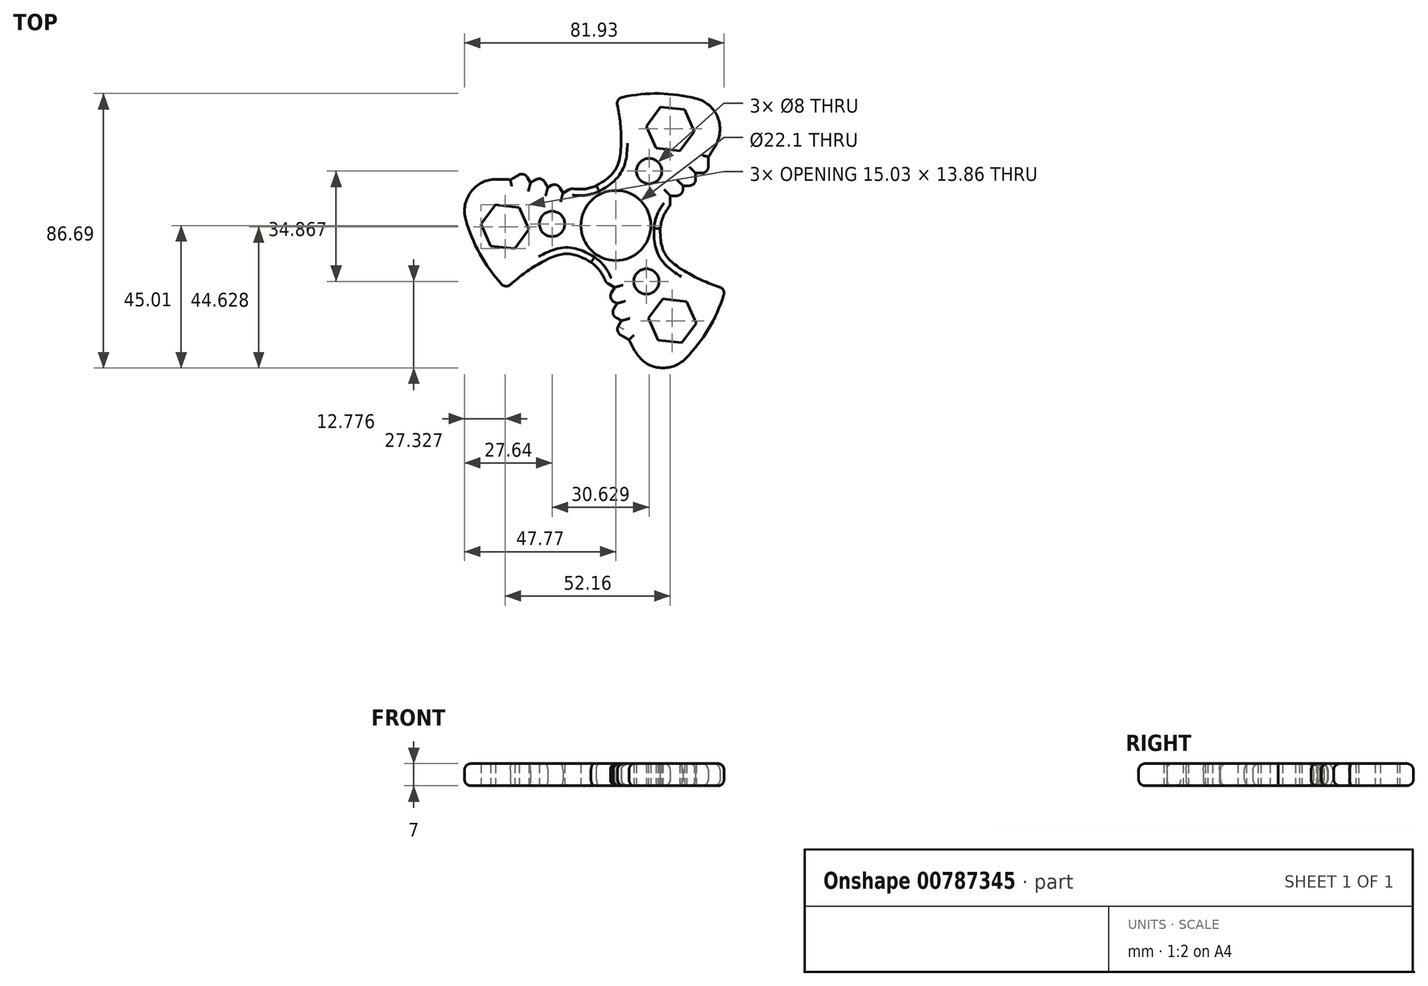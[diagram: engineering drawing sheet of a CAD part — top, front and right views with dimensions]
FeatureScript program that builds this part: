
annotation { "Feature Type Name" : "Feature", "Feature Type Description" : "" }
export const myFeature = defineFeature(function(context is Context, id is Id, definition is map)
    precondition{}
    {
        {
            var Q0;
            Q0=qCreatedBy(makeId("Top.planeOp"),FACE);
            var sketch = newSketch(context, id + "F0", { "sketchPlane" : qUnion([Q0])});
            skCircle(sketch, "E0", {"center": v(0, 0) * mm, "radius": 14 * mm});
            skArc(sketch, "E1", {"start": v(0, 14) * mm, "mid": v(1.66, 27) * mm, "end": v(0, 40) * mm});
            skPoint(sketch, "E2", {"position": v(0, 14) * mm});
            skPoint(sketch, "E3", {"position": v(0, 40) * mm});
            skLineSegment(sketch, "E4", {"start": v(0, 0) * mm, "end": v(36, 36) * mm, "construction": true});
            skPoint(sketch, "E5", {"position": v(36, 36) * mm});
            skArc(sketch, "E6.trimOffspring", {"start": v(36, 36) * mm, "mid": v(18.37, 41.37) * mm, "end": v(0, 40) * mm});
            skArc(sketch, "E7.trimOffspring", {"start": v(12.46, 6.39) * mm, "mid": v(27.14, 18.88) * mm, "end": v(36, 36) * mm});
            skCircle(sketch, "E8", {"center": v(0, 0) * mm, "radius": 11.05 * mm});
            skCircle(sketch, "E9.cCircle", {"center": v(17.17, 30.5) * mm, "radius": 6.55 * mm, "construction": true});
            skLineSegment(sketch, "E9.0", {"start": v(24.68, 29.66) * mm, "end": v(20.2, 23.57) * mm});
            skLineSegment(sketch, "E9.1", {"start": v(20.2, 23.57) * mm, "end": v(12.68, 24.4) * mm});
            skLineSegment(sketch, "E9.2", {"start": v(12.68, 24.4) * mm, "end": v(9.65, 31.33) * mm});
            skLineSegment(sketch, "E9.3", {"start": v(9.65, 31.33) * mm, "end": v(14.13, 37.42) * mm});
            skLineSegment(sketch, "E9.4", {"start": v(14.13, 37.42) * mm, "end": v(21.65, 36.59) * mm});
            skLineSegment(sketch, "E9.5", {"start": v(21.65, 36.59) * mm, "end": v(24.68, 29.66) * mm});
            skPoint(sketch, "E9.0.midPoint", {"position": v(22.44, 26.61) * mm});
            skCircle(sketch, "E10", {"center": v(10.5, 17.18) * mm, "radius": 4 * mm});
            skLineSegment(sketch, "E11", {"start": v(18, 38) * mm, "end": v(17.17, 30.5) * mm, "construction": true});
            skLineSegment(sketch, "E12", {"start": v(0, 14) * mm, "end": v(12.46, 6.39) * mm, "construction": true});
            skLineSegment(sketch, "E13", {"start": v(6.23, 10.2) * mm, "end": v(14.77, 24.17) * mm, "construction": true});
            skLineSegment(sketch, "E14", {"start": v(36, 36) * mm, "end": v(0, 40) * mm, "construction": true});
            skLineSegment(sketch, "E15.1.0", {"start": v(-27.48, -1.22) * mm, "end": v(-31.96, -7.3) * mm});
            skLineSegment(sketch, "E15.1.1", {"start": v(-41.9, -3.41) * mm, "end": v(-35, -0.38) * mm, "construction": true});
            skCircle(sketch, "E15.1.2", {"center": v(-20.13, 0.5) * mm, "radius": 4 * mm});
            skCircle(sketch, "E15.1.3", {"center": v(-35, -0.38) * mm, "radius": 6.55 * mm, "construction": true});
            skArc(sketch, "E15.1.4", {"start": v(-49.18, 13.18) * mm, "mid": v(-45.02, -4.77) * mm, "end": v(-34.64, -20) * mm});
            skArc(sketch, "E15.1.5", {"start": v(-11.76, 7.6) * mm, "mid": v(-29.92, 14.06) * mm, "end": v(-49.18, 13.18) * mm});
            skLineSegment(sketch, "E15.1.6", {"start": v(0, 0) * mm, "end": v(-49.18, 13.18) * mm, "construction": true});
            skPoint(sketch, "E15.1.7", {"position": v(-34.27, 6.13) * mm});
            skLineSegment(sketch, "E15.1.8", {"start": v(-30.51, 5.71) * mm, "end": v(-27.48, -1.22) * mm});
            skLineSegment(sketch, "E15.1.9", {"start": v(-49.18, 13.18) * mm, "end": v(-34.64, -20) * mm, "construction": true});
            skPoint(sketch, "E15.1.10", {"position": v(-49.18, 13.18) * mm});
            skLineSegment(sketch, "E15.1.11", {"start": v(-11.94, 0.3) * mm, "end": v(-28.32, 0.7) * mm, "construction": true});
            skLineSegment(sketch, "E15.1.12", {"start": v(-31.96, -7.3) * mm, "end": v(-39.48, -6.47) * mm});
            skLineSegment(sketch, "E15.1.13", {"start": v(-39.48, -6.47) * mm, "end": v(-42.51, 0.45) * mm});
            skLineSegment(sketch, "E15.1.14", {"start": v(-38.03, 6.55) * mm, "end": v(-30.51, 5.71) * mm});
            skLineSegment(sketch, "E15.1.15", {"start": v(-42.51, 0.45) * mm, "end": v(-38.03, 6.55) * mm});
            skArc(sketch, "E15.1.16", {"start": v(-12.12, -7) * mm, "mid": v(-24.21, -12.06) * mm, "end": v(-34.64, -20) * mm});
            skLineSegment(sketch, "E15.2.0", {"start": v(14.8, -23.19) * mm, "end": v(22.3, -24.02) * mm});
            skLineSegment(sketch, "E15.2.1", {"start": v(23.9, -34.59) * mm, "end": v(17.83, -30.11) * mm, "construction": true});
            skCircle(sketch, "E15.2.2", {"center": v(9.63, -17.68) * mm, "radius": 4 * mm});
            skCircle(sketch, "E15.2.3", {"center": v(17.83, -30.11) * mm, "radius": 6.55 * mm, "construction": true});
            skArc(sketch, "E15.2.4", {"start": v(13.18, -49.18) * mm, "mid": v(26.64, -36.6) * mm, "end": v(34.64, -20) * mm});
            skArc(sketch, "E15.2.5", {"start": v(-0.7, -13.98) * mm, "mid": v(2.78, -32.94) * mm, "end": v(13.18, -49.18) * mm});
            skLineSegment(sketch, "E15.2.6", {"start": v(0, 0) * mm, "end": v(13.18, -49.18) * mm, "construction": true});
            skPoint(sketch, "E15.2.7", {"position": v(11.83, -32.74) * mm});
            skLineSegment(sketch, "E15.2.8", {"start": v(10.31, -29.28) * mm, "end": v(14.8, -23.19) * mm});
            skLineSegment(sketch, "E15.2.9", {"start": v(13.18, -49.18) * mm, "end": v(34.64, -20) * mm, "construction": true});
            skPoint(sketch, "E15.2.10", {"position": v(13.18, -49.18) * mm});
            skLineSegment(sketch, "E15.2.11", {"start": v(5.71, -10.5) * mm, "end": v(13.55, -24.88) * mm, "construction": true});
            skLineSegment(sketch, "E15.2.12", {"start": v(22.3, -24.02) * mm, "end": v(25.34, -30.95) * mm});
            skLineSegment(sketch, "E15.2.13", {"start": v(25.34, -30.95) * mm, "end": v(20.86, -37.04) * mm});
            skLineSegment(sketch, "E15.2.14", {"start": v(13.35, -36.2) * mm, "end": v(10.31, -29.28) * mm});
            skLineSegment(sketch, "E15.2.15", {"start": v(20.86, -37.04) * mm, "end": v(13.35, -36.2) * mm});
            skArc(sketch, "E15.2.16", {"start": v(12.12, -7) * mm, "mid": v(22.55, -14.94) * mm, "end": v(34.64, -20) * mm});
            skLineSegment(sketch, "E16", {"start": v(12.46, 6.39) * mm, "end": v(17.17, 6.39) * mm});
            skLineSegment(sketch, "E17", {"start": v(17.17, 6.39) * mm, "end": v(17.17, 9.39) * mm});
            skLineSegment(sketch, "E18", {"start": v(17.17, 9.39) * mm, "end": v(21.17, 9.39) * mm});
            skLineSegment(sketch, "E19", {"start": v(21.17, 9.39) * mm, "end": v(21.17, 12.58) * mm});
            skLineSegment(sketch, "E20", {"start": v(21.17, 12.58) * mm, "end": v(25.17, 12.58) * mm});
            skLineSegment(sketch, "E21", {"start": v(25.17, 12.58) * mm, "end": v(25.17, 16.55) * mm});
            skLineSegment(sketch, "E22", {"start": v(25.17, 16.55) * mm, "end": v(29.17, 16.55) * mm});
            skLineSegment(sketch, "E23", {"start": v(29.17, 16.55) * mm, "end": v(29.17, 21.62) * mm});
            skLineSegment(sketch, "E24.1.0", {"start": v(-11.76, 7.6) * mm, "end": v(-14.12, 11.67) * mm});
            skLineSegment(sketch, "E24.1.1", {"start": v(-14.12, 11.67) * mm, "end": v(-16.71, 10.17) * mm});
            skLineSegment(sketch, "E24.1.2", {"start": v(-16.71, 10.17) * mm, "end": v(-18.71, 13.64) * mm});
            skLineSegment(sketch, "E24.1.3", {"start": v(-18.71, 13.64) * mm, "end": v(-21.48, 12.04) * mm});
            skLineSegment(sketch, "E24.1.4", {"start": v(-21.48, 12.04) * mm, "end": v(-23.48, 15.5) * mm});
            skLineSegment(sketch, "E24.1.5", {"start": v(-23.48, 15.5) * mm, "end": v(-26.92, 13.52) * mm});
            skLineSegment(sketch, "E24.1.6", {"start": v(-26.92, 13.52) * mm, "end": v(-28.92, 16.98) * mm});
            skLineSegment(sketch, "E24.1.7", {"start": v(-28.92, 16.98) * mm, "end": v(-33.3, 14.45) * mm});
            skLineSegment(sketch, "E24.2.0", {"start": v(-0.7, -13.98) * mm, "end": v(-3.05, -18.06) * mm});
            skLineSegment(sketch, "E24.2.1", {"start": v(-3.05, -18.06) * mm, "end": v(-0.45, -19.56) * mm});
            skLineSegment(sketch, "E24.2.2", {"start": v(-0.45, -19.56) * mm, "end": v(-2.45, -23.03) * mm});
            skLineSegment(sketch, "E24.2.3", {"start": v(-2.45, -23.03) * mm, "end": v(0.31, -24.62) * mm});
            skLineSegment(sketch, "E24.2.4", {"start": v(0.31, -24.62) * mm, "end": v(-1.69, -28.09) * mm});
            skLineSegment(sketch, "E24.2.5", {"start": v(-1.69, -28.09) * mm, "end": v(1.75, -30.07) * mm});
            skLineSegment(sketch, "E24.2.6", {"start": v(1.75, -30.07) * mm, "end": v(-0.25, -33.54) * mm});
            skLineSegment(sketch, "E24.2.7", {"start": v(-0.25, -33.54) * mm, "end": v(4.14, -36.07) * mm});
            skSolve(sketch);
        }
        {
            var Q0;
            Q0=qSketchRegion(id+"F0",true);
            extrude(context, id + "F1", {"entities" : qUnion([Q0]), "depth" : 7 * mm, "offsetDistance" : 25 * mm});
        }
        {
            var Q0;
            Q0=makeQuery(id+"FwcY3XiP80TZzvs_1.opPattern","COPY",EDGE,{"derivedFrom":makeQuery(id+"F1.opExtrude","SWEPT_EDGE",EDGE,{"disambiguationData":[OSD([sQuery(id+"F0.wireOp",EDGE,"E6.trimOffspring"),sQuery(id+"F0.wireOp",EDGE,"E7.trimOffspring")])]}),"instanceName":"1"});
            var Q1;
            Q1=makeQuery(id+"FwcY3XiP80TZzvs_1.opPattern","COPY",EDGE,{"derivedFrom":makeQuery(id+"F1.opExtrude","SWEPT_EDGE",EDGE,{"disambiguationData":[OSD([sQuery(id+"F0.wireOp",EDGE,"E6.trimOffspring"),sQuery(id+"F0.wireOp",EDGE,"E7.trimOffspring")])]}),"instanceName":"3"});
            var Q2;
            Q2=makeQuery(id+"FwcY3XiP80TZzvs_1.opPattern","COPY",EDGE,{"derivedFrom":makeQuery(id+"F1.opExtrude","SWEPT_EDGE",EDGE,{"disambiguationData":[OSD([sQuery(id+"F0.wireOp",EDGE,"E6.trimOffspring"),sQuery(id+"F0.wireOp",EDGE,"E7.trimOffspring")])]}),"instanceName":"2"});
            var Q3;
            Q3=makeQuery(id+"F1.opExtrude","SWEPT_EDGE",EDGE,{"disambiguationData":[OSD([sQuery(id+"F0.wireOp",EDGE,"E6.trimOffspring"),sQuery(id+"F0.wireOp",EDGE,"E7.trimOffspring")])]});
            var Q4;
            Q4=makeQuery(id+"F1.opExtrude","SWEPT_EDGE",EDGE,{"disambiguationData":[OSD([sQuery(id+"F0.wireOp",EDGE,"E15.1.4"),sQuery(id+"F0.wireOp",EDGE,"E15.1.5")])]});
            var Q5;
            Q5=makeQuery(id+"F1.opExtrude","SWEPT_EDGE",EDGE,{"disambiguationData":[OSD([sQuery(id+"F0.wireOp",EDGE,"E15.2.4"),sQuery(id+"F0.wireOp",EDGE,"E15.2.5")])]});
            fillet(context, id + "F2", {"entities" : qUnion([Q0, Q1, Q2, Q3, Q4, Q5]), "radius" : 10 * mm, "tangentPropagation" : true, "allowEdgeOverflow" : false});
        }
        {
            var Q0;
            Q0=makeQuery(id+"FwcY3XiP80TZzvs_1.opPattern","COPY",EDGE,{"derivedFrom":makeQuery(id+"F1.opExtrude","SWEPT_EDGE",EDGE,{"disambiguationData":[OSD([sQuery(id+"F0.wireOp",EDGE,"E1"),sQuery(id+"F0.wireOp",EDGE,"E6.trimOffspring")])]}),"instanceName":"1"});
            var Q1;
            Q1=makeQuery(id+"F1.opExtrude","SWEPT_EDGE",EDGE,{"disambiguationData":[OSD([sQuery(id+"F0.wireOp",EDGE,"E1"),sQuery(id+"F0.wireOp",EDGE,"E6.trimOffspring")])]});
            var Q2;
            Q2=makeQuery(id+"FwcY3XiP80TZzvs_1.opPattern","COPY",EDGE,{"derivedFrom":makeQuery(id+"F1.opExtrude","SWEPT_EDGE",EDGE,{"disambiguationData":[OSD([sQuery(id+"F0.wireOp",EDGE,"E1"),sQuery(id+"F0.wireOp",EDGE,"E6.trimOffspring")])]}),"instanceName":"3"});
            var Q3;
            Q3=makeQuery(id+"FwcY3XiP80TZzvs_1.opPattern","COPY",EDGE,{"derivedFrom":makeQuery(id+"F1.opExtrude","SWEPT_EDGE",EDGE,{"disambiguationData":[OSD([sQuery(id+"F0.wireOp",EDGE,"E1"),sQuery(id+"F0.wireOp",EDGE,"E6.trimOffspring")])]}),"instanceName":"2"});
            var Q4;
            Q4=makeQuery(id+"F1.opExtrude","SWEPT_EDGE",EDGE,{"disambiguationData":[OSD([sQuery(id+"F0.wireOp",EDGE,"E15.1.4"),sQuery(id+"F0.wireOp",EDGE,"E15.1.16")])]});
            var Q5;
            Q5=makeQuery(id+"F1.opExtrude","SWEPT_EDGE",EDGE,{"disambiguationData":[OSD([sQuery(id+"F0.wireOp",EDGE,"E15.2.4"),sQuery(id+"F0.wireOp",EDGE,"E15.2.16")])]});
            fillet(context, id + "F3", {"entities" : qUnion([Q0, Q1, Q2, Q3, Q4, Q5]), "radius" : 2 * mm, "tangentPropagation" : true, "allowEdgeOverflow" : false});
        }
        {
            var Q0;
            Q0=makeQuery(id+"F1.opExtrude","SWEPT_EDGE",EDGE,{"disambiguationData":[OSD([sQuery(id+"F0.wireOp",EDGE,"E0"),sQuery(id+"F0.wireOp",EDGE,"E15.1.16")])]});
            var Q1;
            Q1=makeQuery(id+"F1.opExtrude","SWEPT_EDGE",EDGE,{"disambiguationData":[OSD([sQuery(id+"F0.wireOp",EDGE,"E0"),sQuery(id+"F0.wireOp",EDGE,"E15.2.5")])]});
            var Q2;
            Q2=makeQuery(id+"F1.opExtrude","SWEPT_EDGE",EDGE,{"disambiguationData":[OSD([sQuery(id+"F0.wireOp",EDGE,"E0"),sQuery(id+"F0.wireOp",EDGE,"E15.1.5")])]});
            var Q3;
            Q3=makeQuery(id+"F1.opExtrude","SWEPT_EDGE",EDGE,{"disambiguationData":[OSD([sQuery(id+"F0.wireOp",EDGE,"E0"),sQuery(id+"F0.wireOp",EDGE,"E1")])]});
            var Q4;
            Q4=makeQuery(id+"F1.opExtrude","SWEPT_EDGE",EDGE,{"disambiguationData":[OSD([sQuery(id+"F0.wireOp",EDGE,"E0"),sQuery(id+"F0.wireOp",EDGE,"E7.trimOffspring")])]});
            var Q5;
            Q5=makeQuery(id+"F1.opExtrude","SWEPT_EDGE",EDGE,{"disambiguationData":[OSD([sQuery(id+"F0.wireOp",EDGE,"E0"),sQuery(id+"F0.wireOp",EDGE,"E15.2.16")])]});
            fillet(context, id + "F4", {"entities" : qUnion([Q0, Q1, Q2, Q3, Q4, Q5]), "radius" : 16 * mm, "rho" : .6, "crossSection" : FilletCrossSection.CONIC, "allowEdgeOverflow" : false});
        }
        {
            var Q0;
            Q0=makeQuery(id+"F1.opExtrude","CAP_EDGE",EDGE,{"disambiguationData":[OSD([sQuery(id+"F0.wireOp",EDGE,"E15.1.4")])],"isStart":false});
            var Q1;
            Q1=makeQuery(id+"F1.opExtrude","CAP_EDGE",EDGE,{"disambiguationData":[OSD([sQuery(id+"F0.wireOp",EDGE,"E6.trimOffspring")])],"isStart":false});
            var Q2;
            Q2=makeQuery(id+"F1.opExtrude","CAP_EDGE",EDGE,{"disambiguationData":[OSD([sQuery(id+"F0.wireOp",EDGE,"E15.2.4")])],"isStart":false});
            var Q3;
            Q3=makeQuery(id+"F1.opExtrude","CAP_EDGE",EDGE,{"disambiguationData":[OSD([sQuery(id+"F0.wireOp",EDGE,"b6dc6e87-022c-4587-a6bb-449be63d97bc.2.0")])],"isStart":false});
            var Q4;
            Q4=makeQuery(id+"F1.opExtrude","CAP_EDGE",EDGE,{"disambiguationData":[OSD([sQuery(id+"F0.wireOp",EDGE,"b6dc6e87-022c-4587-a6bb-449be63d97bc.2.2")])],"isStart":false});
            var Q5;
            Q5=makeQuery(id+"F1.opExtrude","CAP_EDGE",EDGE,{"disambiguationData":[OSD([sQuery(id+"F0.wireOp",EDGE,"b6dc6e87-022c-4587-a6bb-449be63d97bc.2.1")])],"isStart":false});
            var Q6;
            Q6=makeQuery(id+"F1.opExtrude","CAP_EDGE",EDGE,{"disambiguationData":[OSD([sQuery(id+"F0.wireOp",EDGE,"b6dc6e87-022c-4587-a6bb-449be63d97bc.2.3")])],"isStart":false});
            var Q7;
            {var subQ0=sQuery(id+"F0.wireOp",EDGE,"E15.2.5");var subQ1=sQuery(id+"F0.wireOp",EDGE,"E15.2.4");Q7=makeQuery(id+"F2.opFillet","BLEND_EDGE",EDGE,{"blendedFrom":[makeQuery(id+"F1.opExtrude","SWEPT_EDGE",EDGE,{"disambiguationData":[OSD([subQ1,subQ0])]}),makeQuery(id+"F1.opExtrude","CAP_FACE",FACE,{"disambiguationData":[OSD([sQuery(id+"F0.wireOp",EDGE,"E0"),sQuery(id+"F0.wireOp",EDGE,"E1"),sQuery(id+"F0.wireOp",EDGE,"E6.trimOffspring"),sQuery(id+"F0.wireOp",EDGE,"E7.trimOffspring"),sQuery(id+"F0.wireOp",EDGE,"E9.0"),sQuery(id+"F0.wireOp",EDGE,"E9.1"),sQuery(id+"F0.wireOp",EDGE,"E9.2"),sQuery(id+"F0.wireOp",EDGE,"E9.3"),sQuery(id+"F0.wireOp",EDGE,"E9.4"),sQuery(id+"F0.wireOp",EDGE,"E9.5"),sQuery(id+"F0.wireOp",EDGE,"E10"),sQuery(id+"F0.wireOp",EDGE,"E15.1.0"),sQuery(id+"F0.wireOp",EDGE,"E15.1.2"),sQuery(id+"F0.wireOp",EDGE,"E15.1.4"),sQuery(id+"F0.wireOp",EDGE,"E15.1.5"),sQuery(id+"F0.wireOp",EDGE,"E15.1.8"),sQuery(id+"F0.wireOp",EDGE,"E15.1.12"),sQuery(id+"F0.wireOp",EDGE,"E15.1.13"),sQuery(id+"F0.wireOp",EDGE,"E15.1.14"),sQuery(id+"F0.wireOp",EDGE,"E15.1.15"),sQuery(id+"F0.wireOp",EDGE,"E15.1.16"),sQuery(id+"F0.wireOp",EDGE,"E15.2.0"),sQuery(id+"F0.wireOp",EDGE,"E15.2.2"),subQ1,subQ0,sQuery(id+"F0.wireOp",EDGE,"E15.2.8"),sQuery(id+"F0.wireOp",EDGE,"E15.2.12"),sQuery(id+"F0.wireOp",EDGE,"E15.2.13"),sQuery(id+"F0.wireOp",EDGE,"E15.2.14"),sQuery(id+"F0.wireOp",EDGE,"E15.2.15"),sQuery(id+"F0.wireOp",EDGE,"E15.2.16"),sQuery(id+"F0.wireOp",EDGE,"dOVvf4ZY-hfaG-VCGh-6djX-qI10KFZVYham"),sQuery(id+"F0.wireOp",EDGE,"qjIoeBWy-CccR-NzYj-1DTf-gikf3EaqEeLr"),sQuery(id+"F0.wireOp",EDGE,"2TvMucum-B2Yi-Opv7-W324-o2eA7hxeLcYX"),sQuery(id+"F0.wireOp",EDGE,"7mXubkyq-BCgf-0Zro-0wdY-kL4kbCmWapzR"),sQuery(id+"F0.wireOp",EDGE,"b6dc6e87-022c-4587-a6bb-449be63d97bc.1.0"),sQuery(id+"F0.wireOp",EDGE,"b6dc6e87-022c-4587-a6bb-449be63d97bc.1.1"),sQuery(id+"F0.wireOp",EDGE,"b6dc6e87-022c-4587-a6bb-449be63d97bc.1.2"),sQuery(id+"F0.wireOp",EDGE,"b6dc6e87-022c-4587-a6bb-449be63d97bc.1.3"),sQuery(id+"F0.wireOp",EDGE,"b6dc6e87-022c-4587-a6bb-449be63d97bc.2.0"),sQuery(id+"F0.wireOp",EDGE,"b6dc6e87-022c-4587-a6bb-449be63d97bc.2.1"),sQuery(id+"F0.wireOp",EDGE,"b6dc6e87-022c-4587-a6bb-449be63d97bc.2.2"),sQuery(id+"F0.wireOp",EDGE,"b6dc6e87-022c-4587-a6bb-449be63d97bc.2.3")])],"isStart":true})],"blendedInto":[makeQuery(id+"F1.opExtrude","CAP_FACE",FACE,{"disambiguationData":[OSD([sQuery(id+"F0.wireOp",EDGE,"E0"),sQuery(id+"F0.wireOp",EDGE,"E1"),sQuery(id+"F0.wireOp",EDGE,"E6.trimOffspring"),sQuery(id+"F0.wireOp",EDGE,"E7.trimOffspring"),sQuery(id+"F0.wireOp",EDGE,"E9.0"),sQuery(id+"F0.wireOp",EDGE,"E9.1"),sQuery(id+"F0.wireOp",EDGE,"E9.2"),sQuery(id+"F0.wireOp",EDGE,"E9.3"),sQuery(id+"F0.wireOp",EDGE,"E9.4"),sQuery(id+"F0.wireOp",EDGE,"E9.5"),sQuery(id+"F0.wireOp",EDGE,"E10"),sQuery(id+"F0.wireOp",EDGE,"E15.1.0"),sQuery(id+"F0.wireOp",EDGE,"E15.1.2"),sQuery(id+"F0.wireOp",EDGE,"E15.1.4"),sQuery(id+"F0.wireOp",EDGE,"E15.1.5"),sQuery(id+"F0.wireOp",EDGE,"E15.1.8"),sQuery(id+"F0.wireOp",EDGE,"E15.1.12"),sQuery(id+"F0.wireOp",EDGE,"E15.1.13"),sQuery(id+"F0.wireOp",EDGE,"E15.1.14"),sQuery(id+"F0.wireOp",EDGE,"E15.1.15"),sQuery(id+"F0.wireOp",EDGE,"E15.1.16"),sQuery(id+"F0.wireOp",EDGE,"E15.2.0"),sQuery(id+"F0.wireOp",EDGE,"E15.2.2"),subQ1,subQ0,sQuery(id+"F0.wireOp",EDGE,"E15.2.8"),sQuery(id+"F0.wireOp",EDGE,"E15.2.12"),sQuery(id+"F0.wireOp",EDGE,"E15.2.13"),sQuery(id+"F0.wireOp",EDGE,"E15.2.14"),sQuery(id+"F0.wireOp",EDGE,"E15.2.15"),sQuery(id+"F0.wireOp",EDGE,"E15.2.16"),sQuery(id+"F0.wireOp",EDGE,"dOVvf4ZY-hfaG-VCGh-6djX-qI10KFZVYham"),sQuery(id+"F0.wireOp",EDGE,"qjIoeBWy-CccR-NzYj-1DTf-gikf3EaqEeLr"),sQuery(id+"F0.wireOp",EDGE,"2TvMucum-B2Yi-Opv7-W324-o2eA7hxeLcYX"),sQuery(id+"F0.wireOp",EDGE,"7mXubkyq-BCgf-0Zro-0wdY-kL4kbCmWapzR"),sQuery(id+"F0.wireOp",EDGE,"b6dc6e87-022c-4587-a6bb-449be63d97bc.1.0"),sQuery(id+"F0.wireOp",EDGE,"b6dc6e87-022c-4587-a6bb-449be63d97bc.1.1"),sQuery(id+"F0.wireOp",EDGE,"b6dc6e87-022c-4587-a6bb-449be63d97bc.1.2"),sQuery(id+"F0.wireOp",EDGE,"b6dc6e87-022c-4587-a6bb-449be63d97bc.1.3"),sQuery(id+"F0.wireOp",EDGE,"b6dc6e87-022c-4587-a6bb-449be63d97bc.2.0"),sQuery(id+"F0.wireOp",EDGE,"b6dc6e87-022c-4587-a6bb-449be63d97bc.2.1"),sQuery(id+"F0.wireOp",EDGE,"b6dc6e87-022c-4587-a6bb-449be63d97bc.2.2"),sQuery(id+"F0.wireOp",EDGE,"b6dc6e87-022c-4587-a6bb-449be63d97bc.2.3")])],"isStart":true})]});}
            var Q8;
            Q8=makeQuery(id+"F1.opExtrude","CAP_EDGE",EDGE,{"disambiguationData":[OSD([sQuery(id+"F0.wireOp",EDGE,"E15.1.4")])],"isStart":true});
            var Q9;
            Q9=makeQuery(id+"F1.opExtrude","CAP_EDGE",EDGE,{"disambiguationData":[OSD([sQuery(id+"F0.wireOp",EDGE,"E6.trimOffspring")])],"isStart":true});
            var Q10;
            Q10=makeQuery(id+"F1.opExtrude","CAP_EDGE",EDGE,{"disambiguationData":[OSD([sQuery(id+"F0.wireOp",EDGE,"b6dc6e87-022c-4587-a6bb-449be63d97bc.1.3")])],"isStart":true});
            var Q11;
            Q11=makeQuery(id+"F1.opExtrude","CAP_EDGE",EDGE,{"disambiguationData":[OSD([sQuery(id+"F0.wireOp",EDGE,"b6dc6e87-022c-4587-a6bb-449be63d97bc.1.2")])],"isStart":true});
            var Q12;
            Q12=makeQuery(id+"F1.opExtrude","CAP_EDGE",EDGE,{"disambiguationData":[OSD([sQuery(id+"F0.wireOp",EDGE,"b6dc6e87-022c-4587-a6bb-449be63d97bc.1.1")])],"isStart":true});
            var Q13;
            Q13=makeQuery(id+"F1.opExtrude","CAP_EDGE",EDGE,{"disambiguationData":[OSD([sQuery(id+"F0.wireOp",EDGE,"b6dc6e87-022c-4587-a6bb-449be63d97bc.1.0")])],"isStart":true});
            var Q14;
            Q14=makeQuery(id+"F1.opExtrude","CAP_EDGE",EDGE,{"disambiguationData":[OSD([sQuery(id+"F0.wireOp",EDGE,"b6dc6e87-022c-4587-a6bb-449be63d97bc.2.3")])],"isStart":true});
            var Q15;
            Q15=makeQuery(id+"F1.opExtrude","CAP_EDGE",EDGE,{"disambiguationData":[OSD([sQuery(id+"F0.wireOp",EDGE,"b6dc6e87-022c-4587-a6bb-449be63d97bc.2.2")])],"isStart":true});
            var Q16;
            Q16=makeQuery(id+"F1.opExtrude","CAP_EDGE",EDGE,{"disambiguationData":[OSD([sQuery(id+"F0.wireOp",EDGE,"b6dc6e87-022c-4587-a6bb-449be63d97bc.2.1")])],"isStart":true});
            var Q17;
            Q17=makeQuery(id+"F1.opExtrude","CAP_EDGE",EDGE,{"disambiguationData":[OSD([sQuery(id+"F0.wireOp",EDGE,"b6dc6e87-022c-4587-a6bb-449be63d97bc.2.0")])],"isStart":true});
            var Q18;
            Q18=makeQuery(id+"F1.opExtrude","CAP_EDGE",EDGE,{"disambiguationData":[OSD([sQuery(id+"F0.wireOp",EDGE,"qjIoeBWy-CccR-NzYj-1DTf-gikf3EaqEeLr")])],"isStart":true});
            var Q19;
            Q19=makeQuery(id+"F1.opExtrude","CAP_EDGE",EDGE,{"disambiguationData":[OSD([sQuery(id+"F0.wireOp",EDGE,"dOVvf4ZY-hfaG-VCGh-6djX-qI10KFZVYham")])],"isStart":true});
            var Q20;
            Q20=makeQuery(id+"F1.opExtrude","CAP_EDGE",EDGE,{"disambiguationData":[OSD([sQuery(id+"F0.wireOp",EDGE,"2TvMucum-B2Yi-Opv7-W324-o2eA7hxeLcYX")])],"isStart":true});
            var Q21;
            Q21=makeQuery(id+"F1.opExtrude","CAP_EDGE",EDGE,{"disambiguationData":[OSD([sQuery(id+"F0.wireOp",EDGE,"7mXubkyq-BCgf-0Zro-0wdY-kL4kbCmWapzR")])],"isStart":true});
            var Q22;
            Q22=makeQuery(id+"F1.opExtrude","CAP_EDGE",EDGE,{"disambiguationData":[OSD([sQuery(id+"F0.wireOp",EDGE,"7mXubkyq-BCgf-0Zro-0wdY-kL4kbCmWapzR")])],"isStart":false});
            var Q23;
            Q23=makeQuery(id+"F1.opExtrude","CAP_EDGE",EDGE,{"disambiguationData":[OSD([sQuery(id+"F0.wireOp",EDGE,"2TvMucum-B2Yi-Opv7-W324-o2eA7hxeLcYX")])],"isStart":false});
            var Q24;
            Q24=makeQuery(id+"F1.opExtrude","CAP_EDGE",EDGE,{"disambiguationData":[OSD([sQuery(id+"F0.wireOp",EDGE,"dOVvf4ZY-hfaG-VCGh-6djX-qI10KFZVYham")])],"isStart":false});
            var Q25;
            Q25=makeQuery(id+"F1.opExtrude","CAP_EDGE",EDGE,{"disambiguationData":[OSD([sQuery(id+"F0.wireOp",EDGE,"b6dc6e87-022c-4587-a6bb-449be63d97bc.1.3")])],"isStart":false});
            var Q26;
            Q26=makeQuery(id+"F1.opExtrude","CAP_EDGE",EDGE,{"disambiguationData":[OSD([sQuery(id+"F0.wireOp",EDGE,"b6dc6e87-022c-4587-a6bb-449be63d97bc.1.1")])],"isStart":false});
            var Q27;
            Q27=makeQuery(id+"F1.opExtrude","CAP_EDGE",EDGE,{"disambiguationData":[OSD([sQuery(id+"F0.wireOp",EDGE,"b6dc6e87-022c-4587-a6bb-449be63d97bc.1.0")])],"isStart":false});
            var Q28;
            Q28=makeQuery(id+"F1.opExtrude","CAP_EDGE",EDGE,{"disambiguationData":[OSD([sQuery(id+"F0.wireOp",EDGE,"b6dc6e87-022c-4587-a6bb-449be63d97bc.1.2")])],"isStart":false});
            fillet(context, id + "F5", {"entities" : qUnion([Q0, Q1, Q2, Q3, Q4, Q5, Q6, Q7, Q8, Q9, Q10, Q11, Q12, Q13, Q14, Q15, Q16, Q17, Q18, Q19, Q20, Q21, Q22, Q23, Q24, Q25, Q26, Q27, Q28]), "radius" : 2 * mm, "tangentPropagation" : true, "allowEdgeOverflow" : false});
        }
        {
            var Q0;
            Q0=makeQuery(id+"F1.opExtrude","CAP_EDGE",EDGE,{"disambiguationData":[OSD([sQuery(id+"F0.wireOp",EDGE,"E24.2.2")])],"isStart":false});
            var Q1;
            Q1=makeQuery(id+"F1.opExtrude","CAP_EDGE",EDGE,{"disambiguationData":[OSD([sQuery(id+"F0.wireOp",EDGE,"E24.2.1")])],"isStart":false});
            var Q2;
            Q2=makeQuery(id+"F1.opExtrude","CAP_EDGE",EDGE,{"disambiguationData":[OSD([sQuery(id+"F0.wireOp",EDGE,"E24.2.3")])],"isStart":false});
            var Q3;
            Q3=makeQuery(id+"F1.opExtrude","CAP_EDGE",EDGE,{"disambiguationData":[OSD([sQuery(id+"F0.wireOp",EDGE,"E24.2.4")])],"isStart":false});
            var Q4;
            Q4=makeQuery(id+"F1.opExtrude","CAP_EDGE",EDGE,{"disambiguationData":[OSD([sQuery(id+"F0.wireOp",EDGE,"E24.2.5")])],"isStart":false});
            var Q5;
            Q5=makeQuery(id+"F1.opExtrude","CAP_EDGE",EDGE,{"disambiguationData":[OSD([sQuery(id+"F0.wireOp",EDGE,"E24.2.6")])],"isStart":false});
            var Q6;
            Q6=makeQuery(id+"F1.opExtrude","CAP_EDGE",EDGE,{"disambiguationData":[OSD([sQuery(id+"F0.wireOp",EDGE,"E24.2.7")])],"isStart":false});
            var Q7;
            {var subQ0=sQuery(id+"F0.wireOp",EDGE,"E24.2.0");var subQ1=sQuery(id+"F0.wireOp",EDGE,"E15.2.5");var subQ2=sQuery(id+"F0.wireOp",EDGE,"E0");Q7=makeQuery(id+"F4.opFillet","BLEND_EDGE",EDGE,{"blendedFrom":[makeQuery(id+"F1.opExtrude","SWEPT_EDGE",EDGE,{"disambiguationData":[OSD([subQ2,subQ1,subQ0])]}),makeQuery(id+"F1.opExtrude","CAP_FACE",FACE,{"disambiguationData":[OSD([subQ2,sQuery(id+"F0.wireOp",EDGE,"E1"),sQuery(id+"F0.wireOp",EDGE,"E6.trimOffspring"),sQuery(id+"F0.wireOp",EDGE,"E7.trimOffspring"),sQuery(id+"F0.wireOp",EDGE,"E8"),sQuery(id+"F0.wireOp",EDGE,"E9.0"),sQuery(id+"F0.wireOp",EDGE,"E9.1"),sQuery(id+"F0.wireOp",EDGE,"E9.2"),sQuery(id+"F0.wireOp",EDGE,"E9.3"),sQuery(id+"F0.wireOp",EDGE,"E9.4"),sQuery(id+"F0.wireOp",EDGE,"E9.5"),sQuery(id+"F0.wireOp",EDGE,"E10"),sQuery(id+"F0.wireOp",EDGE,"E15.1.0"),sQuery(id+"F0.wireOp",EDGE,"E15.1.2"),sQuery(id+"F0.wireOp",EDGE,"E15.1.4"),sQuery(id+"F0.wireOp",EDGE,"E15.1.5"),sQuery(id+"F0.wireOp",EDGE,"E15.1.8"),sQuery(id+"F0.wireOp",EDGE,"E15.1.12"),sQuery(id+"F0.wireOp",EDGE,"E15.1.13"),sQuery(id+"F0.wireOp",EDGE,"E15.1.14"),sQuery(id+"F0.wireOp",EDGE,"E15.1.15"),sQuery(id+"F0.wireOp",EDGE,"E15.1.16"),sQuery(id+"F0.wireOp",EDGE,"E15.2.0"),sQuery(id+"F0.wireOp",EDGE,"E15.2.2"),sQuery(id+"F0.wireOp",EDGE,"E15.2.4"),subQ1,sQuery(id+"F0.wireOp",EDGE,"E15.2.8"),sQuery(id+"F0.wireOp",EDGE,"E15.2.12"),sQuery(id+"F0.wireOp",EDGE,"E15.2.13"),sQuery(id+"F0.wireOp",EDGE,"E15.2.14"),sQuery(id+"F0.wireOp",EDGE,"E15.2.15"),sQuery(id+"F0.wireOp",EDGE,"E15.2.16"),sQuery(id+"F0.wireOp",EDGE,"E16"),sQuery(id+"F0.wireOp",EDGE,"E17"),sQuery(id+"F0.wireOp",EDGE,"E18"),sQuery(id+"F0.wireOp",EDGE,"E19"),sQuery(id+"F0.wireOp",EDGE,"E20"),sQuery(id+"F0.wireOp",EDGE,"E21"),sQuery(id+"F0.wireOp",EDGE,"E22"),sQuery(id+"F0.wireOp",EDGE,"E23"),sQuery(id+"F0.wireOp",EDGE,"E24.1.0"),sQuery(id+"F0.wireOp",EDGE,"E24.1.1"),sQuery(id+"F0.wireOp",EDGE,"E24.1.2"),sQuery(id+"F0.wireOp",EDGE,"E24.1.3"),sQuery(id+"F0.wireOp",EDGE,"E24.1.4"),sQuery(id+"F0.wireOp",EDGE,"E24.1.5"),sQuery(id+"F0.wireOp",EDGE,"E24.1.6"),sQuery(id+"F0.wireOp",EDGE,"E24.1.7"),subQ0,sQuery(id+"F0.wireOp",EDGE,"E24.2.1"),sQuery(id+"F0.wireOp",EDGE,"E24.2.2"),sQuery(id+"F0.wireOp",EDGE,"E24.2.3"),sQuery(id+"F0.wireOp",EDGE,"E24.2.4"),sQuery(id+"F0.wireOp",EDGE,"E24.2.5"),sQuery(id+"F0.wireOp",EDGE,"E24.2.6"),sQuery(id+"F0.wireOp",EDGE,"E24.2.7")])],"isStart":false})],"blendedInto":[makeQuery(id+"F1.opExtrude","CAP_FACE",FACE,{"disambiguationData":[OSD([subQ2,sQuery(id+"F0.wireOp",EDGE,"E1"),sQuery(id+"F0.wireOp",EDGE,"E6.trimOffspring"),sQuery(id+"F0.wireOp",EDGE,"E7.trimOffspring"),sQuery(id+"F0.wireOp",EDGE,"E8"),sQuery(id+"F0.wireOp",EDGE,"E9.0"),sQuery(id+"F0.wireOp",EDGE,"E9.1"),sQuery(id+"F0.wireOp",EDGE,"E9.2"),sQuery(id+"F0.wireOp",EDGE,"E9.3"),sQuery(id+"F0.wireOp",EDGE,"E9.4"),sQuery(id+"F0.wireOp",EDGE,"E9.5"),sQuery(id+"F0.wireOp",EDGE,"E10"),sQuery(id+"F0.wireOp",EDGE,"E15.1.0"),sQuery(id+"F0.wireOp",EDGE,"E15.1.2"),sQuery(id+"F0.wireOp",EDGE,"E15.1.4"),sQuery(id+"F0.wireOp",EDGE,"E15.1.5"),sQuery(id+"F0.wireOp",EDGE,"E15.1.8"),sQuery(id+"F0.wireOp",EDGE,"E15.1.12"),sQuery(id+"F0.wireOp",EDGE,"E15.1.13"),sQuery(id+"F0.wireOp",EDGE,"E15.1.14"),sQuery(id+"F0.wireOp",EDGE,"E15.1.15"),sQuery(id+"F0.wireOp",EDGE,"E15.1.16"),sQuery(id+"F0.wireOp",EDGE,"E15.2.0"),sQuery(id+"F0.wireOp",EDGE,"E15.2.2"),sQuery(id+"F0.wireOp",EDGE,"E15.2.4"),subQ1,sQuery(id+"F0.wireOp",EDGE,"E15.2.8"),sQuery(id+"F0.wireOp",EDGE,"E15.2.12"),sQuery(id+"F0.wireOp",EDGE,"E15.2.13"),sQuery(id+"F0.wireOp",EDGE,"E15.2.14"),sQuery(id+"F0.wireOp",EDGE,"E15.2.15"),sQuery(id+"F0.wireOp",EDGE,"E15.2.16"),sQuery(id+"F0.wireOp",EDGE,"E16"),sQuery(id+"F0.wireOp",EDGE,"E17"),sQuery(id+"F0.wireOp",EDGE,"E18"),sQuery(id+"F0.wireOp",EDGE,"E19"),sQuery(id+"F0.wireOp",EDGE,"E20"),sQuery(id+"F0.wireOp",EDGE,"E21"),sQuery(id+"F0.wireOp",EDGE,"E22"),sQuery(id+"F0.wireOp",EDGE,"E23"),sQuery(id+"F0.wireOp",EDGE,"E24.1.0"),sQuery(id+"F0.wireOp",EDGE,"E24.1.1"),sQuery(id+"F0.wireOp",EDGE,"E24.1.2"),sQuery(id+"F0.wireOp",EDGE,"E24.1.3"),sQuery(id+"F0.wireOp",EDGE,"E24.1.4"),sQuery(id+"F0.wireOp",EDGE,"E24.1.5"),sQuery(id+"F0.wireOp",EDGE,"E24.1.6"),sQuery(id+"F0.wireOp",EDGE,"E24.1.7"),subQ0,sQuery(id+"F0.wireOp",EDGE,"E24.2.1"),sQuery(id+"F0.wireOp",EDGE,"E24.2.2"),sQuery(id+"F0.wireOp",EDGE,"E24.2.3"),sQuery(id+"F0.wireOp",EDGE,"E24.2.4"),sQuery(id+"F0.wireOp",EDGE,"E24.2.5"),sQuery(id+"F0.wireOp",EDGE,"E24.2.6"),sQuery(id+"F0.wireOp",EDGE,"E24.2.7")])],"isStart":false})]});}
            var Q8;
            {var subQ0=sQuery(id+"F0.wireOp",EDGE,"E24.2.0");var subQ1=sQuery(id+"F0.wireOp",EDGE,"E15.2.5");var subQ2=sQuery(id+"F0.wireOp",EDGE,"E0");Q8=makeQuery(id+"F4.opFillet","BLEND_EDGE",EDGE,{"blendedFrom":[makeQuery(id+"F1.opExtrude","SWEPT_EDGE",EDGE,{"disambiguationData":[OSD([subQ2,subQ1,subQ0])]}),makeQuery(id+"F1.opExtrude","CAP_FACE",FACE,{"disambiguationData":[OSD([subQ2,sQuery(id+"F0.wireOp",EDGE,"E1"),sQuery(id+"F0.wireOp",EDGE,"E6.trimOffspring"),sQuery(id+"F0.wireOp",EDGE,"E7.trimOffspring"),sQuery(id+"F0.wireOp",EDGE,"E8"),sQuery(id+"F0.wireOp",EDGE,"E9.0"),sQuery(id+"F0.wireOp",EDGE,"E9.1"),sQuery(id+"F0.wireOp",EDGE,"E9.2"),sQuery(id+"F0.wireOp",EDGE,"E9.3"),sQuery(id+"F0.wireOp",EDGE,"E9.4"),sQuery(id+"F0.wireOp",EDGE,"E9.5"),sQuery(id+"F0.wireOp",EDGE,"E10"),sQuery(id+"F0.wireOp",EDGE,"E15.1.0"),sQuery(id+"F0.wireOp",EDGE,"E15.1.2"),sQuery(id+"F0.wireOp",EDGE,"E15.1.4"),sQuery(id+"F0.wireOp",EDGE,"E15.1.5"),sQuery(id+"F0.wireOp",EDGE,"E15.1.8"),sQuery(id+"F0.wireOp",EDGE,"E15.1.12"),sQuery(id+"F0.wireOp",EDGE,"E15.1.13"),sQuery(id+"F0.wireOp",EDGE,"E15.1.14"),sQuery(id+"F0.wireOp",EDGE,"E15.1.15"),sQuery(id+"F0.wireOp",EDGE,"E15.1.16"),sQuery(id+"F0.wireOp",EDGE,"E15.2.0"),sQuery(id+"F0.wireOp",EDGE,"E15.2.2"),sQuery(id+"F0.wireOp",EDGE,"E15.2.4"),subQ1,sQuery(id+"F0.wireOp",EDGE,"E15.2.8"),sQuery(id+"F0.wireOp",EDGE,"E15.2.12"),sQuery(id+"F0.wireOp",EDGE,"E15.2.13"),sQuery(id+"F0.wireOp",EDGE,"E15.2.14"),sQuery(id+"F0.wireOp",EDGE,"E15.2.15"),sQuery(id+"F0.wireOp",EDGE,"E15.2.16"),sQuery(id+"F0.wireOp",EDGE,"E16"),sQuery(id+"F0.wireOp",EDGE,"E17"),sQuery(id+"F0.wireOp",EDGE,"E18"),sQuery(id+"F0.wireOp",EDGE,"E19"),sQuery(id+"F0.wireOp",EDGE,"E20"),sQuery(id+"F0.wireOp",EDGE,"E21"),sQuery(id+"F0.wireOp",EDGE,"E22"),sQuery(id+"F0.wireOp",EDGE,"E23"),sQuery(id+"F0.wireOp",EDGE,"E24.1.0"),sQuery(id+"F0.wireOp",EDGE,"E24.1.1"),sQuery(id+"F0.wireOp",EDGE,"E24.1.2"),sQuery(id+"F0.wireOp",EDGE,"E24.1.3"),sQuery(id+"F0.wireOp",EDGE,"E24.1.4"),sQuery(id+"F0.wireOp",EDGE,"E24.1.5"),sQuery(id+"F0.wireOp",EDGE,"E24.1.6"),sQuery(id+"F0.wireOp",EDGE,"E24.1.7"),subQ0,sQuery(id+"F0.wireOp",EDGE,"E24.2.1"),sQuery(id+"F0.wireOp",EDGE,"E24.2.2"),sQuery(id+"F0.wireOp",EDGE,"E24.2.3"),sQuery(id+"F0.wireOp",EDGE,"E24.2.4"),sQuery(id+"F0.wireOp",EDGE,"E24.2.5"),sQuery(id+"F0.wireOp",EDGE,"E24.2.6"),sQuery(id+"F0.wireOp",EDGE,"E24.2.7")])],"isStart":true})],"blendedInto":[makeQuery(id+"F1.opExtrude","CAP_FACE",FACE,{"disambiguationData":[OSD([subQ2,sQuery(id+"F0.wireOp",EDGE,"E1"),sQuery(id+"F0.wireOp",EDGE,"E6.trimOffspring"),sQuery(id+"F0.wireOp",EDGE,"E7.trimOffspring"),sQuery(id+"F0.wireOp",EDGE,"E8"),sQuery(id+"F0.wireOp",EDGE,"E9.0"),sQuery(id+"F0.wireOp",EDGE,"E9.1"),sQuery(id+"F0.wireOp",EDGE,"E9.2"),sQuery(id+"F0.wireOp",EDGE,"E9.3"),sQuery(id+"F0.wireOp",EDGE,"E9.4"),sQuery(id+"F0.wireOp",EDGE,"E9.5"),sQuery(id+"F0.wireOp",EDGE,"E10"),sQuery(id+"F0.wireOp",EDGE,"E15.1.0"),sQuery(id+"F0.wireOp",EDGE,"E15.1.2"),sQuery(id+"F0.wireOp",EDGE,"E15.1.4"),sQuery(id+"F0.wireOp",EDGE,"E15.1.5"),sQuery(id+"F0.wireOp",EDGE,"E15.1.8"),sQuery(id+"F0.wireOp",EDGE,"E15.1.12"),sQuery(id+"F0.wireOp",EDGE,"E15.1.13"),sQuery(id+"F0.wireOp",EDGE,"E15.1.14"),sQuery(id+"F0.wireOp",EDGE,"E15.1.15"),sQuery(id+"F0.wireOp",EDGE,"E15.1.16"),sQuery(id+"F0.wireOp",EDGE,"E15.2.0"),sQuery(id+"F0.wireOp",EDGE,"E15.2.2"),sQuery(id+"F0.wireOp",EDGE,"E15.2.4"),subQ1,sQuery(id+"F0.wireOp",EDGE,"E15.2.8"),sQuery(id+"F0.wireOp",EDGE,"E15.2.12"),sQuery(id+"F0.wireOp",EDGE,"E15.2.13"),sQuery(id+"F0.wireOp",EDGE,"E15.2.14"),sQuery(id+"F0.wireOp",EDGE,"E15.2.15"),sQuery(id+"F0.wireOp",EDGE,"E15.2.16"),sQuery(id+"F0.wireOp",EDGE,"E16"),sQuery(id+"F0.wireOp",EDGE,"E17"),sQuery(id+"F0.wireOp",EDGE,"E18"),sQuery(id+"F0.wireOp",EDGE,"E19"),sQuery(id+"F0.wireOp",EDGE,"E20"),sQuery(id+"F0.wireOp",EDGE,"E21"),sQuery(id+"F0.wireOp",EDGE,"E22"),sQuery(id+"F0.wireOp",EDGE,"E23"),sQuery(id+"F0.wireOp",EDGE,"E24.1.0"),sQuery(id+"F0.wireOp",EDGE,"E24.1.1"),sQuery(id+"F0.wireOp",EDGE,"E24.1.2"),sQuery(id+"F0.wireOp",EDGE,"E24.1.3"),sQuery(id+"F0.wireOp",EDGE,"E24.1.4"),sQuery(id+"F0.wireOp",EDGE,"E24.1.5"),sQuery(id+"F0.wireOp",EDGE,"E24.1.6"),sQuery(id+"F0.wireOp",EDGE,"E24.1.7"),subQ0,sQuery(id+"F0.wireOp",EDGE,"E24.2.1"),sQuery(id+"F0.wireOp",EDGE,"E24.2.2"),sQuery(id+"F0.wireOp",EDGE,"E24.2.3"),sQuery(id+"F0.wireOp",EDGE,"E24.2.4"),sQuery(id+"F0.wireOp",EDGE,"E24.2.5"),sQuery(id+"F0.wireOp",EDGE,"E24.2.6"),sQuery(id+"F0.wireOp",EDGE,"E24.2.7")])],"isStart":true})]});}
            var Q9;
            Q9=makeQuery(id+"F1.opExtrude","CAP_EDGE",EDGE,{"disambiguationData":[OSD([sQuery(id+"F0.wireOp",EDGE,"E24.2.1")])],"isStart":true});
            var Q10;
            Q10=makeQuery(id+"F1.opExtrude","CAP_EDGE",EDGE,{"disambiguationData":[OSD([sQuery(id+"F0.wireOp",EDGE,"E24.2.2")])],"isStart":true});
            var Q11;
            Q11=makeQuery(id+"F1.opExtrude","CAP_EDGE",EDGE,{"disambiguationData":[OSD([sQuery(id+"F0.wireOp",EDGE,"E24.2.3")])],"isStart":true});
            var Q12;
            Q12=makeQuery(id+"F1.opExtrude","CAP_EDGE",EDGE,{"disambiguationData":[OSD([sQuery(id+"F0.wireOp",EDGE,"E24.2.4")])],"isStart":true});
            var Q13;
            Q13=makeQuery(id+"F1.opExtrude","CAP_EDGE",EDGE,{"disambiguationData":[OSD([sQuery(id+"F0.wireOp",EDGE,"E24.2.5")])],"isStart":true});
            var Q14;
            Q14=makeQuery(id+"F1.opExtrude","CAP_EDGE",EDGE,{"disambiguationData":[OSD([sQuery(id+"F0.wireOp",EDGE,"E24.2.6")])],"isStart":true});
            var Q15;
            Q15=makeQuery(id+"F1.opExtrude","CAP_EDGE",EDGE,{"disambiguationData":[OSD([sQuery(id+"F0.wireOp",EDGE,"E24.2.7")])],"isStart":true});
            var Q16;
            {var subQ0=sQuery(id+"F0.wireOp",EDGE,"E16");var subQ1=sQuery(id+"F0.wireOp",EDGE,"E7.trimOffspring");var subQ2=sQuery(id+"F0.wireOp",EDGE,"E0");Q16=makeQuery(id+"F4.opFillet","BLEND_EDGE",EDGE,{"blendedFrom":[makeQuery(id+"F1.opExtrude","SWEPT_EDGE",EDGE,{"disambiguationData":[OSD([subQ2,subQ1,subQ0])]}),makeQuery(id+"F1.opExtrude","CAP_FACE",FACE,{"disambiguationData":[OSD([subQ2,sQuery(id+"F0.wireOp",EDGE,"E1"),sQuery(id+"F0.wireOp",EDGE,"E6.trimOffspring"),subQ1,sQuery(id+"F0.wireOp",EDGE,"E8"),sQuery(id+"F0.wireOp",EDGE,"E9.0"),sQuery(id+"F0.wireOp",EDGE,"E9.1"),sQuery(id+"F0.wireOp",EDGE,"E9.2"),sQuery(id+"F0.wireOp",EDGE,"E9.3"),sQuery(id+"F0.wireOp",EDGE,"E9.4"),sQuery(id+"F0.wireOp",EDGE,"E9.5"),sQuery(id+"F0.wireOp",EDGE,"E10"),sQuery(id+"F0.wireOp",EDGE,"E15.1.0"),sQuery(id+"F0.wireOp",EDGE,"E15.1.2"),sQuery(id+"F0.wireOp",EDGE,"E15.1.4"),sQuery(id+"F0.wireOp",EDGE,"E15.1.5"),sQuery(id+"F0.wireOp",EDGE,"E15.1.8"),sQuery(id+"F0.wireOp",EDGE,"E15.1.12"),sQuery(id+"F0.wireOp",EDGE,"E15.1.13"),sQuery(id+"F0.wireOp",EDGE,"E15.1.14"),sQuery(id+"F0.wireOp",EDGE,"E15.1.15"),sQuery(id+"F0.wireOp",EDGE,"E15.1.16"),sQuery(id+"F0.wireOp",EDGE,"E15.2.0"),sQuery(id+"F0.wireOp",EDGE,"E15.2.2"),sQuery(id+"F0.wireOp",EDGE,"E15.2.4"),sQuery(id+"F0.wireOp",EDGE,"E15.2.5"),sQuery(id+"F0.wireOp",EDGE,"E15.2.8"),sQuery(id+"F0.wireOp",EDGE,"E15.2.12"),sQuery(id+"F0.wireOp",EDGE,"E15.2.13"),sQuery(id+"F0.wireOp",EDGE,"E15.2.14"),sQuery(id+"F0.wireOp",EDGE,"E15.2.15"),sQuery(id+"F0.wireOp",EDGE,"E15.2.16"),subQ0,sQuery(id+"F0.wireOp",EDGE,"E17"),sQuery(id+"F0.wireOp",EDGE,"E18"),sQuery(id+"F0.wireOp",EDGE,"E19"),sQuery(id+"F0.wireOp",EDGE,"E20"),sQuery(id+"F0.wireOp",EDGE,"E21"),sQuery(id+"F0.wireOp",EDGE,"E22"),sQuery(id+"F0.wireOp",EDGE,"E23"),sQuery(id+"F0.wireOp",EDGE,"E24.1.0"),sQuery(id+"F0.wireOp",EDGE,"E24.1.1"),sQuery(id+"F0.wireOp",EDGE,"E24.1.2"),sQuery(id+"F0.wireOp",EDGE,"E24.1.3"),sQuery(id+"F0.wireOp",EDGE,"E24.1.4"),sQuery(id+"F0.wireOp",EDGE,"E24.1.5"),sQuery(id+"F0.wireOp",EDGE,"E24.1.6"),sQuery(id+"F0.wireOp",EDGE,"E24.1.7"),sQuery(id+"F0.wireOp",EDGE,"E24.2.0"),sQuery(id+"F0.wireOp",EDGE,"E24.2.1"),sQuery(id+"F0.wireOp",EDGE,"E24.2.2"),sQuery(id+"F0.wireOp",EDGE,"E24.2.3"),sQuery(id+"F0.wireOp",EDGE,"E24.2.4"),sQuery(id+"F0.wireOp",EDGE,"E24.2.5"),sQuery(id+"F0.wireOp",EDGE,"E24.2.6"),sQuery(id+"F0.wireOp",EDGE,"E24.2.7")])],"isStart":false})],"blendedInto":[makeQuery(id+"F1.opExtrude","CAP_FACE",FACE,{"disambiguationData":[OSD([subQ2,sQuery(id+"F0.wireOp",EDGE,"E1"),sQuery(id+"F0.wireOp",EDGE,"E6.trimOffspring"),subQ1,sQuery(id+"F0.wireOp",EDGE,"E8"),sQuery(id+"F0.wireOp",EDGE,"E9.0"),sQuery(id+"F0.wireOp",EDGE,"E9.1"),sQuery(id+"F0.wireOp",EDGE,"E9.2"),sQuery(id+"F0.wireOp",EDGE,"E9.3"),sQuery(id+"F0.wireOp",EDGE,"E9.4"),sQuery(id+"F0.wireOp",EDGE,"E9.5"),sQuery(id+"F0.wireOp",EDGE,"E10"),sQuery(id+"F0.wireOp",EDGE,"E15.1.0"),sQuery(id+"F0.wireOp",EDGE,"E15.1.2"),sQuery(id+"F0.wireOp",EDGE,"E15.1.4"),sQuery(id+"F0.wireOp",EDGE,"E15.1.5"),sQuery(id+"F0.wireOp",EDGE,"E15.1.8"),sQuery(id+"F0.wireOp",EDGE,"E15.1.12"),sQuery(id+"F0.wireOp",EDGE,"E15.1.13"),sQuery(id+"F0.wireOp",EDGE,"E15.1.14"),sQuery(id+"F0.wireOp",EDGE,"E15.1.15"),sQuery(id+"F0.wireOp",EDGE,"E15.1.16"),sQuery(id+"F0.wireOp",EDGE,"E15.2.0"),sQuery(id+"F0.wireOp",EDGE,"E15.2.2"),sQuery(id+"F0.wireOp",EDGE,"E15.2.4"),sQuery(id+"F0.wireOp",EDGE,"E15.2.5"),sQuery(id+"F0.wireOp",EDGE,"E15.2.8"),sQuery(id+"F0.wireOp",EDGE,"E15.2.12"),sQuery(id+"F0.wireOp",EDGE,"E15.2.13"),sQuery(id+"F0.wireOp",EDGE,"E15.2.14"),sQuery(id+"F0.wireOp",EDGE,"E15.2.15"),sQuery(id+"F0.wireOp",EDGE,"E15.2.16"),subQ0,sQuery(id+"F0.wireOp",EDGE,"E17"),sQuery(id+"F0.wireOp",EDGE,"E18"),sQuery(id+"F0.wireOp",EDGE,"E19"),sQuery(id+"F0.wireOp",EDGE,"E20"),sQuery(id+"F0.wireOp",EDGE,"E21"),sQuery(id+"F0.wireOp",EDGE,"E22"),sQuery(id+"F0.wireOp",EDGE,"E23"),sQuery(id+"F0.wireOp",EDGE,"E24.1.0"),sQuery(id+"F0.wireOp",EDGE,"E24.1.1"),sQuery(id+"F0.wireOp",EDGE,"E24.1.2"),sQuery(id+"F0.wireOp",EDGE,"E24.1.3"),sQuery(id+"F0.wireOp",EDGE,"E24.1.4"),sQuery(id+"F0.wireOp",EDGE,"E24.1.5"),sQuery(id+"F0.wireOp",EDGE,"E24.1.6"),sQuery(id+"F0.wireOp",EDGE,"E24.1.7"),sQuery(id+"F0.wireOp",EDGE,"E24.2.0"),sQuery(id+"F0.wireOp",EDGE,"E24.2.1"),sQuery(id+"F0.wireOp",EDGE,"E24.2.2"),sQuery(id+"F0.wireOp",EDGE,"E24.2.3"),sQuery(id+"F0.wireOp",EDGE,"E24.2.4"),sQuery(id+"F0.wireOp",EDGE,"E24.2.5"),sQuery(id+"F0.wireOp",EDGE,"E24.2.6"),sQuery(id+"F0.wireOp",EDGE,"E24.2.7")])],"isStart":false})]});}
            var Q17;
            {var subQ0=sQuery(id+"F0.wireOp",EDGE,"E16");var subQ1=sQuery(id+"F0.wireOp",EDGE,"E7.trimOffspring");var subQ2=sQuery(id+"F0.wireOp",EDGE,"E0");Q17=makeQuery(id+"F4.opFillet","BLEND_EDGE",EDGE,{"blendedFrom":[makeQuery(id+"F1.opExtrude","SWEPT_EDGE",EDGE,{"disambiguationData":[OSD([subQ2,subQ1,subQ0])]}),makeQuery(id+"F1.opExtrude","CAP_FACE",FACE,{"disambiguationData":[OSD([subQ2,sQuery(id+"F0.wireOp",EDGE,"E1"),sQuery(id+"F0.wireOp",EDGE,"E6.trimOffspring"),subQ1,sQuery(id+"F0.wireOp",EDGE,"E8"),sQuery(id+"F0.wireOp",EDGE,"E9.0"),sQuery(id+"F0.wireOp",EDGE,"E9.1"),sQuery(id+"F0.wireOp",EDGE,"E9.2"),sQuery(id+"F0.wireOp",EDGE,"E9.3"),sQuery(id+"F0.wireOp",EDGE,"E9.4"),sQuery(id+"F0.wireOp",EDGE,"E9.5"),sQuery(id+"F0.wireOp",EDGE,"E10"),sQuery(id+"F0.wireOp",EDGE,"E15.1.0"),sQuery(id+"F0.wireOp",EDGE,"E15.1.2"),sQuery(id+"F0.wireOp",EDGE,"E15.1.4"),sQuery(id+"F0.wireOp",EDGE,"E15.1.5"),sQuery(id+"F0.wireOp",EDGE,"E15.1.8"),sQuery(id+"F0.wireOp",EDGE,"E15.1.12"),sQuery(id+"F0.wireOp",EDGE,"E15.1.13"),sQuery(id+"F0.wireOp",EDGE,"E15.1.14"),sQuery(id+"F0.wireOp",EDGE,"E15.1.15"),sQuery(id+"F0.wireOp",EDGE,"E15.1.16"),sQuery(id+"F0.wireOp",EDGE,"E15.2.0"),sQuery(id+"F0.wireOp",EDGE,"E15.2.2"),sQuery(id+"F0.wireOp",EDGE,"E15.2.4"),sQuery(id+"F0.wireOp",EDGE,"E15.2.5"),sQuery(id+"F0.wireOp",EDGE,"E15.2.8"),sQuery(id+"F0.wireOp",EDGE,"E15.2.12"),sQuery(id+"F0.wireOp",EDGE,"E15.2.13"),sQuery(id+"F0.wireOp",EDGE,"E15.2.14"),sQuery(id+"F0.wireOp",EDGE,"E15.2.15"),sQuery(id+"F0.wireOp",EDGE,"E15.2.16"),subQ0,sQuery(id+"F0.wireOp",EDGE,"E17"),sQuery(id+"F0.wireOp",EDGE,"E18"),sQuery(id+"F0.wireOp",EDGE,"E19"),sQuery(id+"F0.wireOp",EDGE,"E20"),sQuery(id+"F0.wireOp",EDGE,"E21"),sQuery(id+"F0.wireOp",EDGE,"E22"),sQuery(id+"F0.wireOp",EDGE,"E23"),sQuery(id+"F0.wireOp",EDGE,"E24.1.0"),sQuery(id+"F0.wireOp",EDGE,"E24.1.1"),sQuery(id+"F0.wireOp",EDGE,"E24.1.2"),sQuery(id+"F0.wireOp",EDGE,"E24.1.3"),sQuery(id+"F0.wireOp",EDGE,"E24.1.4"),sQuery(id+"F0.wireOp",EDGE,"E24.1.5"),sQuery(id+"F0.wireOp",EDGE,"E24.1.6"),sQuery(id+"F0.wireOp",EDGE,"E24.1.7"),sQuery(id+"F0.wireOp",EDGE,"E24.2.0"),sQuery(id+"F0.wireOp",EDGE,"E24.2.1"),sQuery(id+"F0.wireOp",EDGE,"E24.2.2"),sQuery(id+"F0.wireOp",EDGE,"E24.2.3"),sQuery(id+"F0.wireOp",EDGE,"E24.2.4"),sQuery(id+"F0.wireOp",EDGE,"E24.2.5"),sQuery(id+"F0.wireOp",EDGE,"E24.2.6"),sQuery(id+"F0.wireOp",EDGE,"E24.2.7")])],"isStart":true})],"blendedInto":[makeQuery(id+"F1.opExtrude","CAP_FACE",FACE,{"disambiguationData":[OSD([subQ2,sQuery(id+"F0.wireOp",EDGE,"E1"),sQuery(id+"F0.wireOp",EDGE,"E6.trimOffspring"),subQ1,sQuery(id+"F0.wireOp",EDGE,"E8"),sQuery(id+"F0.wireOp",EDGE,"E9.0"),sQuery(id+"F0.wireOp",EDGE,"E9.1"),sQuery(id+"F0.wireOp",EDGE,"E9.2"),sQuery(id+"F0.wireOp",EDGE,"E9.3"),sQuery(id+"F0.wireOp",EDGE,"E9.4"),sQuery(id+"F0.wireOp",EDGE,"E9.5"),sQuery(id+"F0.wireOp",EDGE,"E10"),sQuery(id+"F0.wireOp",EDGE,"E15.1.0"),sQuery(id+"F0.wireOp",EDGE,"E15.1.2"),sQuery(id+"F0.wireOp",EDGE,"E15.1.4"),sQuery(id+"F0.wireOp",EDGE,"E15.1.5"),sQuery(id+"F0.wireOp",EDGE,"E15.1.8"),sQuery(id+"F0.wireOp",EDGE,"E15.1.12"),sQuery(id+"F0.wireOp",EDGE,"E15.1.13"),sQuery(id+"F0.wireOp",EDGE,"E15.1.14"),sQuery(id+"F0.wireOp",EDGE,"E15.1.15"),sQuery(id+"F0.wireOp",EDGE,"E15.1.16"),sQuery(id+"F0.wireOp",EDGE,"E15.2.0"),sQuery(id+"F0.wireOp",EDGE,"E15.2.2"),sQuery(id+"F0.wireOp",EDGE,"E15.2.4"),sQuery(id+"F0.wireOp",EDGE,"E15.2.5"),sQuery(id+"F0.wireOp",EDGE,"E15.2.8"),sQuery(id+"F0.wireOp",EDGE,"E15.2.12"),sQuery(id+"F0.wireOp",EDGE,"E15.2.13"),sQuery(id+"F0.wireOp",EDGE,"E15.2.14"),sQuery(id+"F0.wireOp",EDGE,"E15.2.15"),sQuery(id+"F0.wireOp",EDGE,"E15.2.16"),subQ0,sQuery(id+"F0.wireOp",EDGE,"E17"),sQuery(id+"F0.wireOp",EDGE,"E18"),sQuery(id+"F0.wireOp",EDGE,"E19"),sQuery(id+"F0.wireOp",EDGE,"E20"),sQuery(id+"F0.wireOp",EDGE,"E21"),sQuery(id+"F0.wireOp",EDGE,"E22"),sQuery(id+"F0.wireOp",EDGE,"E23"),sQuery(id+"F0.wireOp",EDGE,"E24.1.0"),sQuery(id+"F0.wireOp",EDGE,"E24.1.1"),sQuery(id+"F0.wireOp",EDGE,"E24.1.2"),sQuery(id+"F0.wireOp",EDGE,"E24.1.3"),sQuery(id+"F0.wireOp",EDGE,"E24.1.4"),sQuery(id+"F0.wireOp",EDGE,"E24.1.5"),sQuery(id+"F0.wireOp",EDGE,"E24.1.6"),sQuery(id+"F0.wireOp",EDGE,"E24.1.7"),sQuery(id+"F0.wireOp",EDGE,"E24.2.0"),sQuery(id+"F0.wireOp",EDGE,"E24.2.1"),sQuery(id+"F0.wireOp",EDGE,"E24.2.2"),sQuery(id+"F0.wireOp",EDGE,"E24.2.3"),sQuery(id+"F0.wireOp",EDGE,"E24.2.4"),sQuery(id+"F0.wireOp",EDGE,"E24.2.5"),sQuery(id+"F0.wireOp",EDGE,"E24.2.6"),sQuery(id+"F0.wireOp",EDGE,"E24.2.7")])],"isStart":true})]});}
            var Q18;
            Q18=makeQuery(id+"F1.opExtrude","CAP_EDGE",EDGE,{"disambiguationData":[OSD([sQuery(id+"F0.wireOp",EDGE,"E17")])],"isStart":true});
            var Q19;
            Q19=makeQuery(id+"F1.opExtrude","CAP_EDGE",EDGE,{"disambiguationData":[OSD([sQuery(id+"F0.wireOp",EDGE,"E18")])],"isStart":true});
            var Q20;
            Q20=makeQuery(id+"F1.opExtrude","CAP_EDGE",EDGE,{"disambiguationData":[OSD([sQuery(id+"F0.wireOp",EDGE,"E18")])],"isStart":false});
            var Q21;
            Q21=makeQuery(id+"F1.opExtrude","CAP_EDGE",EDGE,{"disambiguationData":[OSD([sQuery(id+"F0.wireOp",EDGE,"E19")])],"isStart":false});
            var Q22;
            Q22=makeQuery(id+"F1.opExtrude","CAP_EDGE",EDGE,{"disambiguationData":[OSD([sQuery(id+"F0.wireOp",EDGE,"E20")])],"isStart":true});
            var Q23;
            Q23=makeQuery(id+"F1.opExtrude","CAP_EDGE",EDGE,{"disambiguationData":[OSD([sQuery(id+"F0.wireOp",EDGE,"E20")])],"isStart":false});
            var Q24;
            Q24=makeQuery(id+"F1.opExtrude","CAP_EDGE",EDGE,{"disambiguationData":[OSD([sQuery(id+"F0.wireOp",EDGE,"E21")])],"isStart":false});
            var Q25;
            Q25=makeQuery(id+"F1.opExtrude","CAP_EDGE",EDGE,{"disambiguationData":[OSD([sQuery(id+"F0.wireOp",EDGE,"E21")])],"isStart":true});
            var Q26;
            Q26=makeQuery(id+"F1.opExtrude","CAP_EDGE",EDGE,{"disambiguationData":[OSD([sQuery(id+"F0.wireOp",EDGE,"E22")])],"isStart":true});
            var Q27;
            Q27=makeQuery(id+"F1.opExtrude","CAP_EDGE",EDGE,{"disambiguationData":[OSD([sQuery(id+"F0.wireOp",EDGE,"E22")])],"isStart":false});
            var Q28;
            Q28=makeQuery(id+"F1.opExtrude","CAP_EDGE",EDGE,{"disambiguationData":[OSD([sQuery(id+"F0.wireOp",EDGE,"E23")])],"isStart":false});
            var Q29;
            Q29=makeQuery(id+"F1.opExtrude","CAP_EDGE",EDGE,{"disambiguationData":[OSD([sQuery(id+"F0.wireOp",EDGE,"E23")])],"isStart":true});
            var Q30;
            Q30=makeQuery(id+"F1.opExtrude","CAP_EDGE",EDGE,{"disambiguationData":[OSD([sQuery(id+"F0.wireOp",EDGE,"E17")])],"isStart":false});
            var Q31;
            Q31=makeQuery(id+"F1.opExtrude","CAP_EDGE",EDGE,{"disambiguationData":[OSD([sQuery(id+"F0.wireOp",EDGE,"E19")])],"isStart":true});
            var Q32;
            Q32=makeQuery(id+"F1.opExtrude","SWEPT_EDGE",EDGE,{"disambiguationData":[OSD([sQuery(id+"F0.wireOp",EDGE,"E18"),sQuery(id+"F0.wireOp",EDGE,"E19")])]});
            var Q33;
            Q33=makeQuery(id+"F1.opExtrude","SWEPT_EDGE",EDGE,{"disambiguationData":[OSD([sQuery(id+"F0.wireOp",EDGE,"E20"),sQuery(id+"F0.wireOp",EDGE,"E21")])]});
            var Q34;
            Q34=makeQuery(id+"F1.opExtrude","SWEPT_EDGE",EDGE,{"disambiguationData":[OSD([sQuery(id+"F0.wireOp",EDGE,"E22"),sQuery(id+"F0.wireOp",EDGE,"E23")])]});
            var Q35;
            Q35=makeQuery(id+"F4.opFillet","BLEND_EDGE",EDGE,{"blendedFrom":[makeQuery(id+"F1.opExtrude","SWEPT_EDGE",EDGE,{"disambiguationData":[OSD([sQuery(id+"F0.wireOp",EDGE,"E0"),sQuery(id+"F0.wireOp",EDGE,"E7.trimOffspring"),sQuery(id+"F0.wireOp",EDGE,"E16")])]}),makeQuery(id+"F1.opExtrude","SWEPT_FACE",FACE,{"disambiguationData":[OSD([sQuery(id+"F0.wireOp",EDGE,"E17")])]})],"blendedInto":[makeQuery(id+"F1.opExtrude","SWEPT_FACE",FACE,{"disambiguationData":[OSD([sQuery(id+"F0.wireOp",EDGE,"E17")])]})]});
            var Q36;
            Q36=makeQuery(id+"F4.opFillet","BLEND_EDGE",EDGE,{"blendedFrom":[makeQuery(id+"F1.opExtrude","SWEPT_EDGE",EDGE,{"disambiguationData":[OSD([sQuery(id+"F0.wireOp",EDGE,"E0"),sQuery(id+"F0.wireOp",EDGE,"E15.2.5"),sQuery(id+"F0.wireOp",EDGE,"E24.2.0")])]}),makeQuery(id+"F1.opExtrude","SWEPT_FACE",FACE,{"disambiguationData":[OSD([sQuery(id+"F0.wireOp",EDGE,"E24.2.1")])]})],"blendedInto":[makeQuery(id+"F1.opExtrude","SWEPT_FACE",FACE,{"disambiguationData":[OSD([sQuery(id+"F0.wireOp",EDGE,"E24.2.1")])]})]});
            var Q37;
            Q37=makeQuery(id+"F1.opExtrude","SWEPT_EDGE",EDGE,{"disambiguationData":[OSD([sQuery(id+"F0.wireOp",EDGE,"E24.2.2"),sQuery(id+"F0.wireOp",EDGE,"E24.2.3")])]});
            var Q38;
            Q38=makeQuery(id+"F1.opExtrude","SWEPT_EDGE",EDGE,{"disambiguationData":[OSD([sQuery(id+"F0.wireOp",EDGE,"E24.2.4"),sQuery(id+"F0.wireOp",EDGE,"E24.2.5")])]});
            var Q39;
            Q39=makeQuery(id+"F1.opExtrude","SWEPT_EDGE",EDGE,{"disambiguationData":[OSD([sQuery(id+"F0.wireOp",EDGE,"E24.2.6"),sQuery(id+"F0.wireOp",EDGE,"E24.2.7")])]});
            var Q40;
            {var subQ0=sQuery(id+"F0.wireOp",EDGE,"E24.1.0");var subQ1=sQuery(id+"F0.wireOp",EDGE,"E15.1.5");var subQ2=sQuery(id+"F0.wireOp",EDGE,"E0");Q40=makeQuery(id+"F4.opFillet","BLEND_EDGE",EDGE,{"blendedFrom":[makeQuery(id+"F1.opExtrude","SWEPT_EDGE",EDGE,{"disambiguationData":[OSD([subQ2,subQ1,subQ0])]}),makeQuery(id+"F1.opExtrude","CAP_FACE",FACE,{"disambiguationData":[OSD([subQ2,sQuery(id+"F0.wireOp",EDGE,"E1"),sQuery(id+"F0.wireOp",EDGE,"E6.trimOffspring"),sQuery(id+"F0.wireOp",EDGE,"E7.trimOffspring"),sQuery(id+"F0.wireOp",EDGE,"E8"),sQuery(id+"F0.wireOp",EDGE,"E9.0"),sQuery(id+"F0.wireOp",EDGE,"E9.1"),sQuery(id+"F0.wireOp",EDGE,"E9.2"),sQuery(id+"F0.wireOp",EDGE,"E9.3"),sQuery(id+"F0.wireOp",EDGE,"E9.4"),sQuery(id+"F0.wireOp",EDGE,"E9.5"),sQuery(id+"F0.wireOp",EDGE,"E10"),sQuery(id+"F0.wireOp",EDGE,"E15.1.0"),sQuery(id+"F0.wireOp",EDGE,"E15.1.2"),sQuery(id+"F0.wireOp",EDGE,"E15.1.4"),subQ1,sQuery(id+"F0.wireOp",EDGE,"E15.1.8"),sQuery(id+"F0.wireOp",EDGE,"E15.1.12"),sQuery(id+"F0.wireOp",EDGE,"E15.1.13"),sQuery(id+"F0.wireOp",EDGE,"E15.1.14"),sQuery(id+"F0.wireOp",EDGE,"E15.1.15"),sQuery(id+"F0.wireOp",EDGE,"E15.1.16"),sQuery(id+"F0.wireOp",EDGE,"E15.2.0"),sQuery(id+"F0.wireOp",EDGE,"E15.2.2"),sQuery(id+"F0.wireOp",EDGE,"E15.2.4"),sQuery(id+"F0.wireOp",EDGE,"E15.2.5"),sQuery(id+"F0.wireOp",EDGE,"E15.2.8"),sQuery(id+"F0.wireOp",EDGE,"E15.2.12"),sQuery(id+"F0.wireOp",EDGE,"E15.2.13"),sQuery(id+"F0.wireOp",EDGE,"E15.2.14"),sQuery(id+"F0.wireOp",EDGE,"E15.2.15"),sQuery(id+"F0.wireOp",EDGE,"E15.2.16"),sQuery(id+"F0.wireOp",EDGE,"E16"),sQuery(id+"F0.wireOp",EDGE,"E17"),sQuery(id+"F0.wireOp",EDGE,"E18"),sQuery(id+"F0.wireOp",EDGE,"E19"),sQuery(id+"F0.wireOp",EDGE,"E20"),sQuery(id+"F0.wireOp",EDGE,"E21"),sQuery(id+"F0.wireOp",EDGE,"E22"),sQuery(id+"F0.wireOp",EDGE,"E23"),subQ0,sQuery(id+"F0.wireOp",EDGE,"E24.1.1"),sQuery(id+"F0.wireOp",EDGE,"E24.1.2"),sQuery(id+"F0.wireOp",EDGE,"E24.1.3"),sQuery(id+"F0.wireOp",EDGE,"E24.1.4"),sQuery(id+"F0.wireOp",EDGE,"E24.1.5"),sQuery(id+"F0.wireOp",EDGE,"E24.1.6"),sQuery(id+"F0.wireOp",EDGE,"E24.1.7"),sQuery(id+"F0.wireOp",EDGE,"E24.2.0"),sQuery(id+"F0.wireOp",EDGE,"E24.2.1"),sQuery(id+"F0.wireOp",EDGE,"E24.2.2"),sQuery(id+"F0.wireOp",EDGE,"E24.2.3"),sQuery(id+"F0.wireOp",EDGE,"E24.2.4"),sQuery(id+"F0.wireOp",EDGE,"E24.2.5"),sQuery(id+"F0.wireOp",EDGE,"E24.2.6"),sQuery(id+"F0.wireOp",EDGE,"E24.2.7")])],"isStart":true})],"blendedInto":[makeQuery(id+"F1.opExtrude","CAP_FACE",FACE,{"disambiguationData":[OSD([subQ2,sQuery(id+"F0.wireOp",EDGE,"E1"),sQuery(id+"F0.wireOp",EDGE,"E6.trimOffspring"),sQuery(id+"F0.wireOp",EDGE,"E7.trimOffspring"),sQuery(id+"F0.wireOp",EDGE,"E8"),sQuery(id+"F0.wireOp",EDGE,"E9.0"),sQuery(id+"F0.wireOp",EDGE,"E9.1"),sQuery(id+"F0.wireOp",EDGE,"E9.2"),sQuery(id+"F0.wireOp",EDGE,"E9.3"),sQuery(id+"F0.wireOp",EDGE,"E9.4"),sQuery(id+"F0.wireOp",EDGE,"E9.5"),sQuery(id+"F0.wireOp",EDGE,"E10"),sQuery(id+"F0.wireOp",EDGE,"E15.1.0"),sQuery(id+"F0.wireOp",EDGE,"E15.1.2"),sQuery(id+"F0.wireOp",EDGE,"E15.1.4"),subQ1,sQuery(id+"F0.wireOp",EDGE,"E15.1.8"),sQuery(id+"F0.wireOp",EDGE,"E15.1.12"),sQuery(id+"F0.wireOp",EDGE,"E15.1.13"),sQuery(id+"F0.wireOp",EDGE,"E15.1.14"),sQuery(id+"F0.wireOp",EDGE,"E15.1.15"),sQuery(id+"F0.wireOp",EDGE,"E15.1.16"),sQuery(id+"F0.wireOp",EDGE,"E15.2.0"),sQuery(id+"F0.wireOp",EDGE,"E15.2.2"),sQuery(id+"F0.wireOp",EDGE,"E15.2.4"),sQuery(id+"F0.wireOp",EDGE,"E15.2.5"),sQuery(id+"F0.wireOp",EDGE,"E15.2.8"),sQuery(id+"F0.wireOp",EDGE,"E15.2.12"),sQuery(id+"F0.wireOp",EDGE,"E15.2.13"),sQuery(id+"F0.wireOp",EDGE,"E15.2.14"),sQuery(id+"F0.wireOp",EDGE,"E15.2.15"),sQuery(id+"F0.wireOp",EDGE,"E15.2.16"),sQuery(id+"F0.wireOp",EDGE,"E16"),sQuery(id+"F0.wireOp",EDGE,"E17"),sQuery(id+"F0.wireOp",EDGE,"E18"),sQuery(id+"F0.wireOp",EDGE,"E19"),sQuery(id+"F0.wireOp",EDGE,"E20"),sQuery(id+"F0.wireOp",EDGE,"E21"),sQuery(id+"F0.wireOp",EDGE,"E22"),sQuery(id+"F0.wireOp",EDGE,"E23"),subQ0,sQuery(id+"F0.wireOp",EDGE,"E24.1.1"),sQuery(id+"F0.wireOp",EDGE,"E24.1.2"),sQuery(id+"F0.wireOp",EDGE,"E24.1.3"),sQuery(id+"F0.wireOp",EDGE,"E24.1.4"),sQuery(id+"F0.wireOp",EDGE,"E24.1.5"),sQuery(id+"F0.wireOp",EDGE,"E24.1.6"),sQuery(id+"F0.wireOp",EDGE,"E24.1.7"),sQuery(id+"F0.wireOp",EDGE,"E24.2.0"),sQuery(id+"F0.wireOp",EDGE,"E24.2.1"),sQuery(id+"F0.wireOp",EDGE,"E24.2.2"),sQuery(id+"F0.wireOp",EDGE,"E24.2.3"),sQuery(id+"F0.wireOp",EDGE,"E24.2.4"),sQuery(id+"F0.wireOp",EDGE,"E24.2.5"),sQuery(id+"F0.wireOp",EDGE,"E24.2.6"),sQuery(id+"F0.wireOp",EDGE,"E24.2.7")])],"isStart":true})]});}
            var Q41;
            {var subQ0=sQuery(id+"F0.wireOp",EDGE,"E24.1.0");var subQ1=sQuery(id+"F0.wireOp",EDGE,"E15.1.5");var subQ2=sQuery(id+"F0.wireOp",EDGE,"E0");Q41=makeQuery(id+"F4.opFillet","BLEND_EDGE",EDGE,{"blendedFrom":[makeQuery(id+"F1.opExtrude","SWEPT_EDGE",EDGE,{"disambiguationData":[OSD([subQ2,subQ1,subQ0])]}),makeQuery(id+"F1.opExtrude","CAP_FACE",FACE,{"disambiguationData":[OSD([subQ2,sQuery(id+"F0.wireOp",EDGE,"E1"),sQuery(id+"F0.wireOp",EDGE,"E6.trimOffspring"),sQuery(id+"F0.wireOp",EDGE,"E7.trimOffspring"),sQuery(id+"F0.wireOp",EDGE,"E8"),sQuery(id+"F0.wireOp",EDGE,"E9.0"),sQuery(id+"F0.wireOp",EDGE,"E9.1"),sQuery(id+"F0.wireOp",EDGE,"E9.2"),sQuery(id+"F0.wireOp",EDGE,"E9.3"),sQuery(id+"F0.wireOp",EDGE,"E9.4"),sQuery(id+"F0.wireOp",EDGE,"E9.5"),sQuery(id+"F0.wireOp",EDGE,"E10"),sQuery(id+"F0.wireOp",EDGE,"E15.1.0"),sQuery(id+"F0.wireOp",EDGE,"E15.1.2"),sQuery(id+"F0.wireOp",EDGE,"E15.1.4"),subQ1,sQuery(id+"F0.wireOp",EDGE,"E15.1.8"),sQuery(id+"F0.wireOp",EDGE,"E15.1.12"),sQuery(id+"F0.wireOp",EDGE,"E15.1.13"),sQuery(id+"F0.wireOp",EDGE,"E15.1.14"),sQuery(id+"F0.wireOp",EDGE,"E15.1.15"),sQuery(id+"F0.wireOp",EDGE,"E15.1.16"),sQuery(id+"F0.wireOp",EDGE,"E15.2.0"),sQuery(id+"F0.wireOp",EDGE,"E15.2.2"),sQuery(id+"F0.wireOp",EDGE,"E15.2.4"),sQuery(id+"F0.wireOp",EDGE,"E15.2.5"),sQuery(id+"F0.wireOp",EDGE,"E15.2.8"),sQuery(id+"F0.wireOp",EDGE,"E15.2.12"),sQuery(id+"F0.wireOp",EDGE,"E15.2.13"),sQuery(id+"F0.wireOp",EDGE,"E15.2.14"),sQuery(id+"F0.wireOp",EDGE,"E15.2.15"),sQuery(id+"F0.wireOp",EDGE,"E15.2.16"),sQuery(id+"F0.wireOp",EDGE,"E16"),sQuery(id+"F0.wireOp",EDGE,"E17"),sQuery(id+"F0.wireOp",EDGE,"E18"),sQuery(id+"F0.wireOp",EDGE,"E19"),sQuery(id+"F0.wireOp",EDGE,"E20"),sQuery(id+"F0.wireOp",EDGE,"E21"),sQuery(id+"F0.wireOp",EDGE,"E22"),sQuery(id+"F0.wireOp",EDGE,"E23"),subQ0,sQuery(id+"F0.wireOp",EDGE,"E24.1.1"),sQuery(id+"F0.wireOp",EDGE,"E24.1.2"),sQuery(id+"F0.wireOp",EDGE,"E24.1.3"),sQuery(id+"F0.wireOp",EDGE,"E24.1.4"),sQuery(id+"F0.wireOp",EDGE,"E24.1.5"),sQuery(id+"F0.wireOp",EDGE,"E24.1.6"),sQuery(id+"F0.wireOp",EDGE,"E24.1.7"),sQuery(id+"F0.wireOp",EDGE,"E24.2.0"),sQuery(id+"F0.wireOp",EDGE,"E24.2.1"),sQuery(id+"F0.wireOp",EDGE,"E24.2.2"),sQuery(id+"F0.wireOp",EDGE,"E24.2.3"),sQuery(id+"F0.wireOp",EDGE,"E24.2.4"),sQuery(id+"F0.wireOp",EDGE,"E24.2.5"),sQuery(id+"F0.wireOp",EDGE,"E24.2.6"),sQuery(id+"F0.wireOp",EDGE,"E24.2.7")])],"isStart":false})],"blendedInto":[makeQuery(id+"F1.opExtrude","CAP_FACE",FACE,{"disambiguationData":[OSD([subQ2,sQuery(id+"F0.wireOp",EDGE,"E1"),sQuery(id+"F0.wireOp",EDGE,"E6.trimOffspring"),sQuery(id+"F0.wireOp",EDGE,"E7.trimOffspring"),sQuery(id+"F0.wireOp",EDGE,"E8"),sQuery(id+"F0.wireOp",EDGE,"E9.0"),sQuery(id+"F0.wireOp",EDGE,"E9.1"),sQuery(id+"F0.wireOp",EDGE,"E9.2"),sQuery(id+"F0.wireOp",EDGE,"E9.3"),sQuery(id+"F0.wireOp",EDGE,"E9.4"),sQuery(id+"F0.wireOp",EDGE,"E9.5"),sQuery(id+"F0.wireOp",EDGE,"E10"),sQuery(id+"F0.wireOp",EDGE,"E15.1.0"),sQuery(id+"F0.wireOp",EDGE,"E15.1.2"),sQuery(id+"F0.wireOp",EDGE,"E15.1.4"),subQ1,sQuery(id+"F0.wireOp",EDGE,"E15.1.8"),sQuery(id+"F0.wireOp",EDGE,"E15.1.12"),sQuery(id+"F0.wireOp",EDGE,"E15.1.13"),sQuery(id+"F0.wireOp",EDGE,"E15.1.14"),sQuery(id+"F0.wireOp",EDGE,"E15.1.15"),sQuery(id+"F0.wireOp",EDGE,"E15.1.16"),sQuery(id+"F0.wireOp",EDGE,"E15.2.0"),sQuery(id+"F0.wireOp",EDGE,"E15.2.2"),sQuery(id+"F0.wireOp",EDGE,"E15.2.4"),sQuery(id+"F0.wireOp",EDGE,"E15.2.5"),sQuery(id+"F0.wireOp",EDGE,"E15.2.8"),sQuery(id+"F0.wireOp",EDGE,"E15.2.12"),sQuery(id+"F0.wireOp",EDGE,"E15.2.13"),sQuery(id+"F0.wireOp",EDGE,"E15.2.14"),sQuery(id+"F0.wireOp",EDGE,"E15.2.15"),sQuery(id+"F0.wireOp",EDGE,"E15.2.16"),sQuery(id+"F0.wireOp",EDGE,"E16"),sQuery(id+"F0.wireOp",EDGE,"E17"),sQuery(id+"F0.wireOp",EDGE,"E18"),sQuery(id+"F0.wireOp",EDGE,"E19"),sQuery(id+"F0.wireOp",EDGE,"E20"),sQuery(id+"F0.wireOp",EDGE,"E21"),sQuery(id+"F0.wireOp",EDGE,"E22"),sQuery(id+"F0.wireOp",EDGE,"E23"),subQ0,sQuery(id+"F0.wireOp",EDGE,"E24.1.1"),sQuery(id+"F0.wireOp",EDGE,"E24.1.2"),sQuery(id+"F0.wireOp",EDGE,"E24.1.3"),sQuery(id+"F0.wireOp",EDGE,"E24.1.4"),sQuery(id+"F0.wireOp",EDGE,"E24.1.5"),sQuery(id+"F0.wireOp",EDGE,"E24.1.6"),sQuery(id+"F0.wireOp",EDGE,"E24.1.7"),sQuery(id+"F0.wireOp",EDGE,"E24.2.0"),sQuery(id+"F0.wireOp",EDGE,"E24.2.1"),sQuery(id+"F0.wireOp",EDGE,"E24.2.2"),sQuery(id+"F0.wireOp",EDGE,"E24.2.3"),sQuery(id+"F0.wireOp",EDGE,"E24.2.4"),sQuery(id+"F0.wireOp",EDGE,"E24.2.5"),sQuery(id+"F0.wireOp",EDGE,"E24.2.6"),sQuery(id+"F0.wireOp",EDGE,"E24.2.7")])],"isStart":false})]});}
            var Q42;
            Q42=makeQuery(id+"F1.opExtrude","CAP_EDGE",EDGE,{"disambiguationData":[OSD([sQuery(id+"F0.wireOp",EDGE,"E24.1.7")])],"isStart":true});
            var Q43;
            Q43=makeQuery(id+"F1.opExtrude","CAP_EDGE",EDGE,{"disambiguationData":[OSD([sQuery(id+"F0.wireOp",EDGE,"E24.1.7")])],"isStart":false});
            var Q44;
            Q44=makeQuery(id+"F1.opExtrude","CAP_EDGE",EDGE,{"disambiguationData":[OSD([sQuery(id+"F0.wireOp",EDGE,"E24.1.2")])],"isStart":true});
            var Q45;
            Q45=makeQuery(id+"F1.opExtrude","CAP_EDGE",EDGE,{"disambiguationData":[OSD([sQuery(id+"F0.wireOp",EDGE,"E24.1.3")])],"isStart":true});
            var Q46;
            Q46=makeQuery(id+"F1.opExtrude","CAP_EDGE",EDGE,{"disambiguationData":[OSD([sQuery(id+"F0.wireOp",EDGE,"E24.1.4")])],"isStart":true});
            var Q47;
            Q47=makeQuery(id+"F1.opExtrude","CAP_EDGE",EDGE,{"disambiguationData":[OSD([sQuery(id+"F0.wireOp",EDGE,"E24.1.5")])],"isStart":true});
            var Q48;
            Q48=makeQuery(id+"F1.opExtrude","CAP_EDGE",EDGE,{"disambiguationData":[OSD([sQuery(id+"F0.wireOp",EDGE,"E24.1.6")])],"isStart":true});
            var Q49;
            Q49=makeQuery(id+"F1.opExtrude","CAP_EDGE",EDGE,{"disambiguationData":[OSD([sQuery(id+"F0.wireOp",EDGE,"E24.1.2")])],"isStart":false});
            var Q50;
            Q50=makeQuery(id+"F1.opExtrude","CAP_EDGE",EDGE,{"disambiguationData":[OSD([sQuery(id+"F0.wireOp",EDGE,"E24.1.3")])],"isStart":false});
            var Q51;
            Q51=makeQuery(id+"F1.opExtrude","CAP_EDGE",EDGE,{"disambiguationData":[OSD([sQuery(id+"F0.wireOp",EDGE,"E24.1.4")])],"isStart":false});
            var Q52;
            Q52=makeQuery(id+"F1.opExtrude","CAP_EDGE",EDGE,{"disambiguationData":[OSD([sQuery(id+"F0.wireOp",EDGE,"E24.1.5")])],"isStart":false});
            var Q53;
            Q53=makeQuery(id+"F1.opExtrude","CAP_EDGE",EDGE,{"disambiguationData":[OSD([sQuery(id+"F0.wireOp",EDGE,"E24.1.6")])],"isStart":false});
            var Q54;
            Q54=makeQuery(id+"F1.opExtrude","CAP_EDGE",EDGE,{"disambiguationData":[OSD([sQuery(id+"F0.wireOp",EDGE,"E24.1.1")])],"isStart":true});
            var Q55;
            Q55=makeQuery(id+"F1.opExtrude","CAP_EDGE",EDGE,{"disambiguationData":[OSD([sQuery(id+"F0.wireOp",EDGE,"E24.1.1")])],"isStart":false});
            var Q56;
            Q56=makeQuery(id+"F1.opExtrude","SWEPT_EDGE",EDGE,{"disambiguationData":[OSD([sQuery(id+"F0.wireOp",EDGE,"E24.1.2"),sQuery(id+"F0.wireOp",EDGE,"E24.1.3")])]});
            var Q57;
            Q57=makeQuery(id+"F4.opFillet","BLEND_EDGE",EDGE,{"blendedFrom":[makeQuery(id+"F1.opExtrude","SWEPT_EDGE",EDGE,{"disambiguationData":[OSD([sQuery(id+"F0.wireOp",EDGE,"E0"),sQuery(id+"F0.wireOp",EDGE,"E15.1.5"),sQuery(id+"F0.wireOp",EDGE,"E24.1.0")])]}),makeQuery(id+"F1.opExtrude","SWEPT_FACE",FACE,{"disambiguationData":[OSD([sQuery(id+"F0.wireOp",EDGE,"E24.1.1")])]})],"blendedInto":[makeQuery(id+"F1.opExtrude","SWEPT_FACE",FACE,{"disambiguationData":[OSD([sQuery(id+"F0.wireOp",EDGE,"E24.1.1")])]})]});
            var Q58;
            Q58=makeQuery(id+"F1.opExtrude","SWEPT_EDGE",EDGE,{"disambiguationData":[OSD([sQuery(id+"F0.wireOp",EDGE,"E24.1.4"),sQuery(id+"F0.wireOp",EDGE,"E24.1.5")])]});
            var Q59;
            Q59=makeQuery(id+"F1.opExtrude","SWEPT_EDGE",EDGE,{"disambiguationData":[OSD([sQuery(id+"F0.wireOp",EDGE,"E24.1.6"),sQuery(id+"F0.wireOp",EDGE,"E24.1.7")])]});
            fillet(context, id + "F6", {"entities" : qUnion([Q0, Q1, Q2, Q3, Q4, Q5, Q6, Q7, Q8, Q9, Q10, Q11, Q12, Q13, Q14, Q15, Q16, Q17, Q18, Q19, Q20, Q21, Q22, Q23, Q24, Q25, Q26, Q27, Q28, Q29, Q30, Q31, Q32, Q33, Q34, Q35, Q36, Q37, Q38, Q39, Q40, Q41, Q42, Q43, Q44, Q45, Q46, Q47, Q48, Q49, Q50, Q51, Q52, Q53, Q54, Q55, Q56, Q57, Q58, Q59]), "radius" : 2 * mm, "tangentPropagation" : true, "allowEdgeOverflow" : false});
        }
    });
